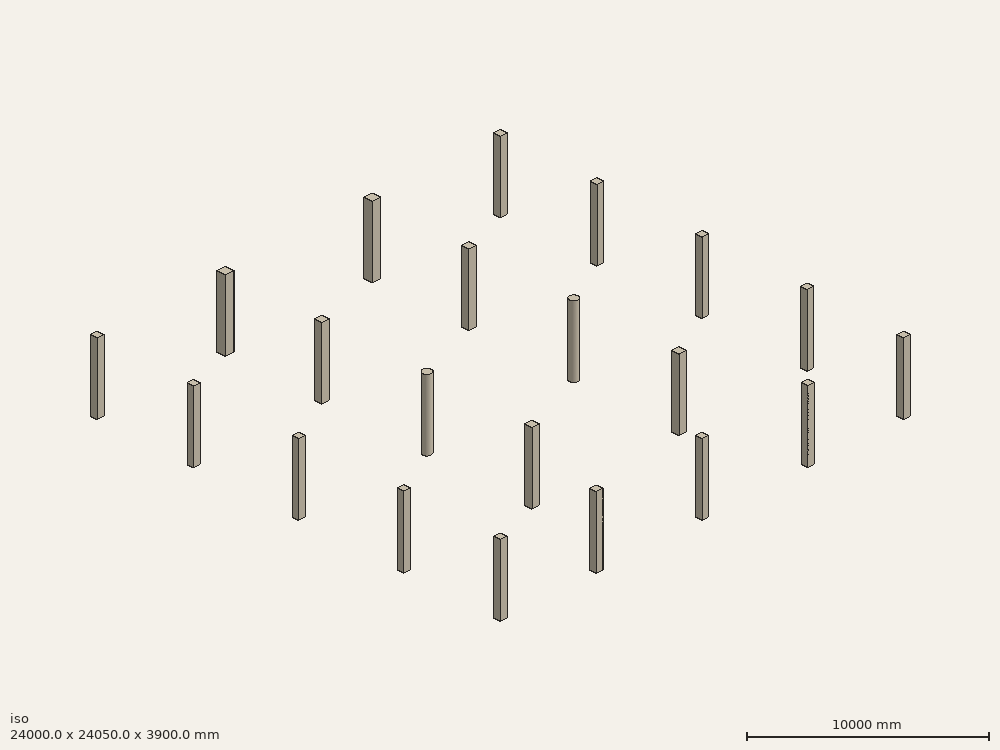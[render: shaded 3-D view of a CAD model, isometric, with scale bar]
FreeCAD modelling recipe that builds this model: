
FCSTD DOCUMENT  (FreeCAD 0.19R24291 (Git))
Label: Hamedan 1403
License: All rights reserved
LicenseURL: http://en.wikipedia.org/wiki/All_rights_reserved
objects: Part::Part2DObjectPython×82, Part::FeaturePython×65, App::FeaturePython×22, App::DocumentObjectGroup×5
note: 333 computed .brp shape members not serialized (recipe doc carries the construction recipe); baked Part::Feature solids carry a one-line shape summary decoded from their .brp

FEATURE [Part::Part2DObjectPython] Line  label="C21_Roof_CenterLine"  # Draft 2D object (typed FeaturePython)
  Area = 0
  ChamferSize = 0
  Closed = false
  End = (0,23600,3900)
  FilletRadius = 0
  Length = 3900
  MakeFace = true
  Points = (2) [(0,23600,0),(0,23600,3900)]
  Start = (0,23600,0)
  Subdivisions = 0
FEATURE [Part::Part2DObjectPython] C40X40_8T20  label="C40X40-8T20"  # Draft 2D object (typed FeaturePython)
  Height = 400
  Width = 400
FEATURE [Part::FeaturePython] Structure  label="C21_Roof"  # Arch/BIM 24 (typed FeaturePython)
  AttacherType = Attacher::AttachEngine3D
  AttachmentOffset = pos=(0,0,0) rot=(0,0,1;1.5708rad)
  Base = -> C40X40_8T20
  FaceMaker = 0
  Height = 3900
  HorizontalArea = 160000
  IfcData = attributes={"GlobalId": {"name": "GlobalId", "type": "IfcGloballyUniqueId", "is_enum": false, "enum_values": []}, "Description": {"... (+438 chars omitted),+1 more (map truncated)
  IfcType = 24
  Length = 0
  MapMode = 7
  MoveBase = false
  MoveWithHost = false
  Nodes = (2) [(0,23600,0),(0,23600,3900)]
  NodesOffset = 0
  Normal = (0,0,0)
  PerimeterLength = 1600
  Placement = pos=(0,23600,0) rot=(0,0,1;1.5708rad)
  PredefinedType = 0
  Support = -> [Line]
  VerticalArea = 6.24e+06
  Width = 100
  combos_load = COMB1 Max=142.9485, 1842.28, 55244.6,COMB10 Max=133.1342, -15451.88, 120563.4,COMB11 Max=142.7589, 32290.33, 117642.28,+33 more (map truncated)
FEATURE [Part::Part2DObjectPython] Line001  label="C22_Roof_CenterLine"  # Draft 2D object (typed FeaturePython)
  Area = 0
  ChamferSize = 0
  Closed = false
  End = (7500,23600,3900)
  FilletRadius = 0
  Length = 3900
  MakeFace = true
  Points = (2) [(7500,23600,0),(7500,23600,3900)]
  Start = (7500,23600,0)
  Subdivisions = 0
FEATURE [Part::Part2DObjectPython] C50X50_12T20  label="C50X50-12T20"  # Draft 2D object (typed FeaturePython)
  Height = 500
  Width = 500
FEATURE [Part::FeaturePython] Structure001  label="C22_Roof"  # Arch/BIM 24 (typed FeaturePython)
  AttacherType = Attacher::AttachEngine3D
  AttachmentOffset = pos=(0,0,0) rot=(0,0,1;1.5708rad)
  Base = -> C50X50_12T20
  FaceMaker = 0
  Height = 3900
  HorizontalArea = 250000
  IfcData = attributes={"GlobalId": {"name": "GlobalId", "type": "IfcGloballyUniqueId", "is_enum": false, "enum_values": []}, "Description": {"... (+438 chars omitted),+1 more (map truncated)
  IfcType = 24
  Length = 0
  MapMode = 7
  MoveBase = false
  MoveWithHost = false
  Nodes = (2) [(7500,23600,0),(7500,23600,3900)]
  NodesOffset = 0
  Normal = (0,0,0)
  PerimeterLength = 2000
  Placement = pos=(7500,23600,0) rot=(0,0,1;1.5708rad)
  PredefinedType = 0
  Support = -> [Line001]
  VerticalArea = 7.8e+06
  Width = 100
  combos_load = COMB1 Max=393.9617, -13954.51, 43208.61,COMB10 Max=364.0775, -60554.94, 217047.53,COMB11 Max=378.5992, 35975, 210039.05,+33 more (map truncated)
FEATURE [Part::Part2DObjectPython] Line002  label="C23_Roof_CenterLine"  # Draft 2D object (typed FeaturePython)
  Area = 0
  ChamferSize = 0
  Closed = false
  End = (16100,23600,3900)
  FilletRadius = 0
  Length = 3900
  MakeFace = true
  Points = (2) [(16100,23600,0),(16100,23600,3900)]
  Start = (16100,23600,0)
  Subdivisions = 0
FEATURE [Part::FeaturePython] Structure002  label="C23_Roof"  # Arch/BIM 24 (typed FeaturePython)
  AttacherType = Attacher::AttachEngine3D
  AttachmentOffset = pos=(0,0,0) rot=(0,0,1;1.5708rad)
  Base = -> C50X50_12T20
  FaceMaker = 0
  Height = 3900
  HorizontalArea = 250000
  IfcData = attributes={"GlobalId": {"name": "GlobalId", "type": "IfcGloballyUniqueId", "is_enum": false, "enum_values": []}, "Description": {"... (+438 chars omitted),+1 more (map truncated)
  IfcType = 24
  Length = 0
  MapMode = 7
  MoveBase = false
  MoveWithHost = false
  Nodes = (2) [(16100,23600,0),(16100,23600,3900)]
  NodesOffset = 0
  Normal = (0,0,0)
  PerimeterLength = 2000
  Placement = pos=(16100,23600,0) rot=(0,0,1;1.5708rad)
  PredefinedType = 0
  Support = -> [Line002]
  VerticalArea = 7.8e+06
  Width = 100
  combos_load = COMB1 Max=396.464, -11533.45, -20754.84,COMB10 Max=367.1221, -68059.63, 140987.04,COMB11 Max=381.1347, 24085.64, 134057.49,+33 more (map truncated)
FEATURE [Part::Part2DObjectPython] Line003  label="C24_Roof_CenterLine"  # Draft 2D object (typed FeaturePython)
  Area = 0
  ChamferSize = 0
  Closed = false
  End = (23600,23600,3900)
  FilletRadius = 0
  Length = 3900
  MakeFace = true
  Points = (2) [(23600,23600,0),(23600,23600,3900)]
  Start = (23600,23600,0)
  Subdivisions = 0
FEATURE [Part::FeaturePython] Structure003  label="C24_Roof"  # Arch/BIM 24 (typed FeaturePython)
  AttacherType = Attacher::AttachEngine3D
  AttachmentOffset = pos=(0,0,0) rot=(0,0,1;1.5708rad)
  Base = -> C40X40_8T20
  FaceMaker = 0
  Height = 3900
  HorizontalArea = 160000
  IfcData = attributes={"GlobalId": {"name": "GlobalId", "type": "IfcGloballyUniqueId", "is_enum": false, "enum_values": []}, "Description": {"... (+438 chars omitted),+1 more (map truncated)
  IfcType = 24
  Length = 0
  MapMode = 7
  MoveBase = false
  MoveWithHost = false
  Nodes = (2) [(23600,23600,0),(23600,23600,3900)]
  NodesOffset = 0
  Normal = (0,0,0)
  PerimeterLength = 1600
  Placement = pos=(23600,23600,0) rot=(0,0,1;1.5708rad)
  PredefinedType = 0
  Support = -> [Line003]
  VerticalArea = 6.24e+06
  Width = 100
  combos_load = COMB1 Max=153.397, 10863.78, -45811.62,COMB10 Max=112.4508, -20618.99, 32383.92,COMB11 Max=123.0217, 21926.74, 29412.84,+33 more (map truncated)
FEATURE [Part::Part2DObjectPython] Line004  label="C17_Roof_CenterLine"  # Draft 2D object (typed FeaturePython)
  Area = 0
  ChamferSize = 0
  Closed = false
  End = (0,17950,3900)
  FilletRadius = 0
  Length = 3900
  MakeFace = true
  Points = (2) [(0,17950,0),(0,17950,3900)]
  Start = (0,17950,0)
  Subdivisions = 0
FEATURE [Part::Part2DObjectPython] C40X40_12T25  label="C40X40-12T25"  # Draft 2D object (typed FeaturePython)
  Height = 400
  Width = 400
FEATURE [Part::FeaturePython] Structure004  label="C17_Roof"  # Arch/BIM 24 (typed FeaturePython)
  AttacherType = Attacher::AttachEngine3D
  AttachmentOffset = pos=(0,0,0) rot=(0,0,1;1.5708rad)
  Base = -> C40X40_12T25
  FaceMaker = 0
  Height = 3900
  HorizontalArea = 160000
  IfcData = attributes={"GlobalId": {"name": "GlobalId", "type": "IfcGloballyUniqueId", "is_enum": false, "enum_values": []}, "Description": {"... (+438 chars omitted),+1 more (map truncated)
  IfcType = 24
  Length = 0
  MapMode = 7
  MoveBase = false
  MoveWithHost = false
  Nodes = (2) [(0,17950,0),(0,17950,3900)]
  NodesOffset = 0
  Normal = (0,0,0)
  PerimeterLength = 1600
  Placement = pos=(0,17950,0) rot=(0,0,1;1.5708rad)
  PredefinedType = 0
  Support = -> [Line004]
  VerticalArea = 6.24e+06
  Width = 100
  combos_load = COMB1 Max=358.911, 57470.57, 72051.06,COMB10 Max=353.0021, 36535.59, 140227.2,COMB11 Max=363.1908, 99735.69, 139905.02,+33 more (map truncated)
FEATURE [Part::Part2DObjectPython] Line005  label="C18_Roof_CenterLine"  # Draft 2D object (typed FeaturePython)
  Area = 0
  ChamferSize = 0
  Closed = false
  End = (7500,17950,3900)
  FilletRadius = 0
  Length = 3900
  MakeFace = true
  Points = (2) [(7500,17950,0),(7500,17950,3900)]
  Start = (7500,17950,0)
  Subdivisions = 0
FEATURE [Part::Part2DObjectPython] C45X45_8T20  label="C45X45-8T20"  # Draft 2D object (typed FeaturePython)
  Height = 450
  Width = 450
FEATURE [Part::FeaturePython] Structure005  label="C18_Roof"  # Arch/BIM 24 (typed FeaturePython)
  AttacherType = Attacher::AttachEngine3D
  AttachmentOffset = pos=(0,0,0) rot=(0,0,1;1.5708rad)
  Base = -> C45X45_8T20
  FaceMaker = 0
  Height = 3900
  HorizontalArea = 202500
  IfcData = attributes={"GlobalId": {"name": "GlobalId", "type": "IfcGloballyUniqueId", "is_enum": false, "enum_values": []}, "Description": {"... (+438 chars omitted),+1 more (map truncated)
  IfcType = 24
  Length = 0
  MapMode = 7
  MoveBase = false
  MoveWithHost = false
  Nodes = (2) [(7500,17950,0),(7500,17950,3900)]
  NodesOffset = 0
  Normal = (0,0,0)
  PerimeterLength = 1800
  Placement = pos=(7500,17950,0) rot=(0,0,1;1.5708rad)
  PredefinedType = 0
  Support = -> [Line005]
  VerticalArea = 7.02e+06
  Width = 100
  combos_load = COMB1 Max=518.4758, 23786.04, 11881.46,COMB10 Max=465.1331, -14749.78, 131616.43,COMB11 Max=464.8478, 69418.5, 127330.18,+33 more (map truncated)
FEATURE [Part::Part2DObjectPython] Line006  label="C19_Roof_CenterLine"  # Draft 2D object (typed FeaturePython)
  Area = 0
  ChamferSize = 0
  Closed = false
  End = (16100,17950,3900)
  FilletRadius = 0
  Length = 3900
  MakeFace = true
  Points = (2) [(16100,17950,0),(16100,17950,3900)]
  Start = (16100,17950,0)
  Subdivisions = 0
FEATURE [Part::FeaturePython] Structure006  label="C19_Roof"  # Arch/BIM 24 (typed FeaturePython)
  AttacherType = Attacher::AttachEngine3D
  AttachmentOffset = pos=(0,0,0) rot=(0,0,1;1.5708rad)
  Base = -> C45X45_8T20
  FaceMaker = 0
  Height = 3900
  HorizontalArea = 202500
  IfcData = attributes={"GlobalId": {"name": "GlobalId", "type": "IfcGloballyUniqueId", "is_enum": false, "enum_values": []}, "Description": {"... (+438 chars omitted),+1 more (map truncated)
  IfcType = 24
  Length = 0
  MapMode = 7
  MoveBase = false
  MoveWithHost = false
  Nodes = (2) [(16100,17950,0),(16100,17950,3900)]
  NodesOffset = 0
  Normal = (0,0,0)
  PerimeterLength = 1800
  Placement = pos=(16100,17950,0) rot=(0,0,1;1.5708rad)
  PredefinedType = 0
  Support = -> [Line006]
  VerticalArea = 7.02e+06
  Width = 100
  combos_load = COMB1 Max=484.4175, 11062.32, -10447.14,COMB10 Max=434.4462, -34199.5, 113962.38,COMB11 Max=429.6664, 44640.41, 111093.37,+33 more (map truncated)
FEATURE [Part::Part2DObjectPython] Line007  label="C20_Roof_CenterLine"  # Draft 2D object (typed FeaturePython)
  Area = 0
  ChamferSize = 0
  Closed = false
  End = (23600,17950,3900)
  FilletRadius = 0
  Length = 3900
  MakeFace = true
  Points = (2) [(23600,17950,0),(23600,17950,3900)]
  Start = (23600,17950,0)
  Subdivisions = 0
FEATURE [Part::FeaturePython] Structure007  label="C20_Roof"  # Arch/BIM 24 (typed FeaturePython)
  AttacherType = Attacher::AttachEngine3D
  AttachmentOffset = pos=(0,0,0) rot=(0,0,1;1.5708rad)
  Base = -> C40X40_8T20
  FaceMaker = 0
  Height = 3900
  HorizontalArea = 160000
  IfcData = attributes={"GlobalId": {"name": "GlobalId", "type": "IfcGloballyUniqueId", "is_enum": false, "enum_values": []}, "Description": {"... (+438 chars omitted),+1 more (map truncated)
  IfcType = 24
  Length = 0
  MapMode = 7
  MoveBase = false
  MoveWithHost = false
  Nodes = (2) [(23600,17950,0),(23600,17950,3900)]
  NodesOffset = 0
  Normal = (0,0,0)
  PerimeterLength = 1600
  Placement = pos=(23600,17950,0) rot=(0,0,1;1.5708rad)
  PredefinedType = 0
  Support = -> [Line007]
  VerticalArea = 6.24e+06
  Width = 100
  combos_load = COMB1 Max=278.7163, 9412.13, -69745.5,COMB10 Max=243.1734, -24585.97, 13268.13,COMB11 Max=240.9121, 26667.65, 11896.36,+33 more (map truncated)
FEATURE [Part::Part2DObjectPython] Line008  label="C10_Roof_CenterLine"  # Draft 2D object (typed FeaturePython)
  Area = 0
  ChamferSize = 0
  Closed = false
  End = (0,11800,3900)
  FilletRadius = 0
  Length = 3900
  MakeFace = true
  Points = (2) [(0,11800,0),(0,11800,3900)]
  Start = (0,11800,0)
  Subdivisions = 0
FEATURE [Part::Part2DObjectPython] C40X40_14T25  label="C40X40-14T25"  # Draft 2D object (typed FeaturePython)
  Height = 400
  Width = 400
FEATURE [Part::FeaturePython] Structure008  label="C10_Roof"  # Arch/BIM 24 (typed FeaturePython)
  AttacherType = Attacher::AttachEngine3D
  AttachmentOffset = pos=(0,0,0) rot=(0,0,1;1.5708rad)
  Base = -> C40X40_14T25
  FaceMaker = 0
  Height = 3900
  HorizontalArea = 160000
  IfcData = attributes={"GlobalId": {"name": "GlobalId", "type": "IfcGloballyUniqueId", "is_enum": false, "enum_values": []}, "Description": {"... (+438 chars omitted),+1 more (map truncated)
  IfcType = 24
  Length = 0
  MapMode = 7
  MoveBase = false
  MoveWithHost = false
  Nodes = (2) [(0,11800,0),(0,11800,3900)]
  NodesOffset = 0
  Normal = (0,0,0)
  PerimeterLength = 1600
  Placement = pos=(0,11800,0) rot=(0,0,1;1.5708rad)
  PredefinedType = 0
  Support = -> [Line008]
  VerticalArea = 6.24e+06
  Width = 100
  combos_load = COMB1 Max=589.8541, -52928.2, 64357.09,COMB10 Max=631.112, -70198.61, 138253.26,COMB11 Max=620.3172, -15825.73, 137456.82,+33 more (map truncated)
FEATURE [Part::Part2DObjectPython] Line009  label="C12_Roof_CenterLine"  # Draft 2D object (typed FeaturePython)
  Area = 0
  ChamferSize = 0
  Closed = false
  End = (7500,11800,3900)
  FilletRadius = 0
  Length = 3900
  MakeFace = true
  Points = (2) [(7500,11800,0),(7500,11800,3900)]
  Start = (7500,11800,0)
  Subdivisions = 0
FEATURE [Part::Part2DObjectPython] Circle  label="CC50-10T20"  # Draft 2D object (typed FeaturePython)
  Area = 196350
  FirstAngle = 0
  LastAngle = 0
  MakeFace = true
  Radius = 250
FEATURE [Part::FeaturePython] Structure009  label="C12_Roof"  # Arch/BIM 24 (typed FeaturePython)
  AttacherType = Attacher::AttachEngine3D
  AttachmentOffset = pos=(0,0,0) rot=(0,0,1;1.5708rad)
  Base = -> Circle
  FaceMaker = 0
  Height = 3900
  HorizontalArea = 196350
  IfcData = attributes={"GlobalId": {"name": "GlobalId", "type": "IfcGloballyUniqueId", "is_enum": false, "enum_values": []}, "Description": {"... (+438 chars omitted),+1 more (map truncated)
  IfcType = 24
  Length = 0
  MapMode = 7
  MoveBase = false
  MoveWithHost = false
  Nodes = (2) [(7500,11800,0),(7500,11800,3900)]
  NodesOffset = 0
  Normal = (0,0,0)
  PerimeterLength = 1570.8
  Placement = pos=(7500,11800,0) rot=(0,0,1;1.5708rad)
  PredefinedType = 0
  Support = -> [Line009]
  VerticalArea = 6.12611e+06
  Width = 100
  combos_load = COMB1 Max=671.1533, -4639.28, -19744.15,COMB10 Max=592.2997, -35909.44, 99080.12,COMB11 Max=588.052, 37558.56, 101179.49,+33 more (map truncated)
FEATURE [Part::Part2DObjectPython] Line010  label="C13_Roof_CenterLine"  # Draft 2D object (typed FeaturePython)
  Area = 0
  ChamferSize = 0
  Closed = false
  End = (16100,11800,3900)
  FilletRadius = 0
  Length = 3900
  MakeFace = true
  Points = (2) [(16100,11800,0),(16100,11800,3900)]
  Start = (16100,11800,0)
  Subdivisions = 0
FEATURE [Part::FeaturePython] Structure010  label="C13_Roof"  # Arch/BIM 24 (typed FeaturePython)
  AttacherType = Attacher::AttachEngine3D
  AttachmentOffset = pos=(0,0,0) rot=(0,0,1;1.5708rad)
  Base = -> Circle
  FaceMaker = 0
  Height = 3900
  HorizontalArea = 196350
  IfcData = attributes={"GlobalId": {"name": "GlobalId", "type": "IfcGloballyUniqueId", "is_enum": false, "enum_values": []}, "Description": {"... (+438 chars omitted),+1 more (map truncated)
  IfcType = 24
  Length = 0
  MapMode = 7
  MoveBase = false
  MoveWithHost = false
  Nodes = (2) [(16100,11800,0),(16100,11800,3900)]
  NodesOffset = 0
  Normal = (0,0,0)
  PerimeterLength = 1570.8
  Placement = pos=(16100,11800,0) rot=(0,0,1;1.5708rad)
  PredefinedType = 0
  Support = -> [Line010]
  VerticalArea = 6.12611e+06
  Width = 100
  combos_load = COMB1 Max=521.6342, 3870.36, -23693.9,COMB10 Max=463.3802, -36720.59, 97522.75,COMB11 Max=463.6235, 33841.58, 97587.97,+33 more (map truncated)
FEATURE [Part::Part2DObjectPython] Line011  label="C14_Roof_CenterLine"  # Draft 2D object (typed FeaturePython)
  Area = 0
  ChamferSize = 0
  Closed = false
  End = (23600,11800,3900)
  FilletRadius = 0
  Length = 3900
  MakeFace = true
  Points = (2) [(23600,11800,0),(23600,11800,3900)]
  Start = (23600,11800,0)
  Subdivisions = 0
FEATURE [Part::FeaturePython] Structure011  label="C14_Roof"  # Arch/BIM 24 (typed FeaturePython)
  AttacherType = Attacher::AttachEngine3D
  AttachmentOffset = pos=(0,0,0) rot=(0,0,1;1.5708rad)
  Base = -> C40X40_8T20
  FaceMaker = 0
  Height = 3900
  HorizontalArea = 160000
  IfcData = attributes={"GlobalId": {"name": "GlobalId", "type": "IfcGloballyUniqueId", "is_enum": false, "enum_values": []}, "Description": {"... (+438 chars omitted),+1 more (map truncated)
  IfcType = 24
  Length = 0
  MapMode = 7
  MoveBase = false
  MoveWithHost = false
  Nodes = (2) [(23600,11800,0),(23600,11800,3900)]
  NodesOffset = 0
  Normal = (0,0,0)
  PerimeterLength = 1600
  Placement = pos=(23600,11800,0) rot=(0,0,1;1.5708rad)
  PredefinedType = 0
  Support = -> [Line011]
  VerticalArea = 6.24e+06
  Width = 100
  combos_load = COMB1 Max=358.2322, 3461.97, -48336.62,COMB10 Max=334.417, -31946.94, 41113.22,COMB11 Max=334.4426, 18858.68, 41094.62,+33 more (map truncated)
FEATURE [Part::Part2DObjectPython] Line012  label="C6_Roof_CenterLine"  # Draft 2D object (typed FeaturePython)
  Area = 0
  ChamferSize = 0
  Closed = false
  End = (0,5650,3900)
  FilletRadius = 0
  Length = 3900
  MakeFace = true
  Points = (2) [(0,5650,0),(0,5650,3900)]
  Start = (0,5650,0)
  Subdivisions = 0
FEATURE [Part::FeaturePython] Structure012  label="C6_Roof"  # Arch/BIM 24 (typed FeaturePython)
  AttacherType = Attacher::AttachEngine3D
  AttachmentOffset = pos=(0,0,0) rot=(0,0,1;1.5708rad)
  Base = -> C40X40_12T25
  FaceMaker = 0
  Height = 3900
  HorizontalArea = 160000
  IfcData = attributes={"GlobalId": {"name": "GlobalId", "type": "IfcGloballyUniqueId", "is_enum": false, "enum_values": []}, "Description": {"... (+438 chars omitted),+1 more (map truncated)
  IfcType = 24
  Length = 0
  MapMode = 7
  MoveBase = false
  MoveWithHost = false
  Nodes = (2) [(0,5650,0),(0,5650,3900)]
  NodesOffset = 0
  Normal = (0,0,0)
  PerimeterLength = 1600
  Placement = pos=(0,5650,0) rot=(0,0,1;1.5708rad)
  PredefinedType = 0
  Support = -> [Line012]
  VerticalArea = 6.24e+06
  Width = 100
  combos_load = COMB1 Max=262.5559, 5891.08, 79097.96,COMB10 Max=251.8265, -15804.53, 150501.97,COMB11 Max=253.791, 43165.94, 152334.32,+33 more (map truncated)
FEATURE [Part::Part2DObjectPython] Line013  label="C7_Roof_CenterLine"  # Draft 2D object (typed FeaturePython)
  Area = 0
  ChamferSize = 0
  Closed = false
  End = (7500,5650,3900)
  FilletRadius = 0
  Length = 3900
  MakeFace = true
  Points = (2) [(7500,5650,0),(7500,5650,3900)]
  Start = (7500,5650,0)
  Subdivisions = 0
FEATURE [Part::FeaturePython] Structure013  label="C7_Roof"  # Arch/BIM 24 (typed FeaturePython)
  AttacherType = Attacher::AttachEngine3D
  AttachmentOffset = pos=(0,0,0) rot=(0,0,1;1.5708rad)
  Base = -> C45X45_8T20
  FaceMaker = 0
  Height = 3900
  HorizontalArea = 202500
  IfcData = attributes={"GlobalId": {"name": "GlobalId", "type": "IfcGloballyUniqueId", "is_enum": false, "enum_values": []}, "Description": {"... (+438 chars omitted),+1 more (map truncated)
  IfcType = 24
  Length = 0
  MapMode = 7
  MoveBase = false
  MoveWithHost = false
  Nodes = (2) [(7500,5650,0),(7500,5650,3900)]
  NodesOffset = 0
  Normal = (0,0,0)
  PerimeterLength = 1800
  Placement = pos=(7500,5650,0) rot=(0,0,1;1.5708rad)
  PredefinedType = 0
  Support = -> [Line013]
  VerticalArea = 7.02e+06
  Width = 100
  combos_load = COMB1 Max=486.3324, 7340.08, 20569.07,COMB10 Max=420.769, -32429.99, 154764.38,COMB11 Max=424.0342, 47843.18, 155600.42,+33 more (map truncated)
FEATURE [Part::Part2DObjectPython] Line014  label="C8_Roof_CenterLine"  # Draft 2D object (typed FeaturePython)
  Area = 0
  ChamferSize = 0
  Closed = false
  End = (16100,5650,3900)
  FilletRadius = 0
  Length = 3900
  MakeFace = true
  Points = (2) [(16100,5650,0),(16100,5650,3900)]
  Start = (16100,5650,0)
  Subdivisions = 0
FEATURE [Part::FeaturePython] Structure014  label="C8_Roof"  # Arch/BIM 24 (typed FeaturePython)
  AttacherType = Attacher::AttachEngine3D
  AttachmentOffset = pos=(0,0,0) rot=(0,0,1;1.5708rad)
  Base = -> C45X45_8T20
  FaceMaker = 0
  Height = 3900
  HorizontalArea = 202500
  IfcData = attributes={"GlobalId": {"name": "GlobalId", "type": "IfcGloballyUniqueId", "is_enum": false, "enum_values": []}, "Description": {"... (+438 chars omitted),+1 more (map truncated)
  IfcType = 24
  Length = 0
  MapMode = 7
  MoveBase = false
  MoveWithHost = false
  Nodes = (2) [(16100,5650,0),(16100,5650,3900)]
  NodesOffset = 0
  Normal = (0,0,0)
  PerimeterLength = 1800
  Placement = pos=(16100,5650,0) rot=(0,0,1;1.5708rad)
  PredefinedType = 0
  Support = -> [Line014]
  VerticalArea = 7.02e+06
  Width = 100
  combos_load = COMB1 Max=488.6288, 6936.79, -6872.61,COMB10 Max=436.9461, -33228.07, 129912.68,COMB11 Max=440.3998, 43388.79, 134096.59,+33 more (map truncated)
FEATURE [Part::Part2DObjectPython] Line015  label="C9_Roof_CenterLine"  # Draft 2D object (typed FeaturePython)
  Area = 0
  ChamferSize = 0
  Closed = false
  End = (23600,5650,3900)
  FilletRadius = 0
  Length = 3900
  MakeFace = true
  Points = (2) [(23600,5650,0),(23600,5650,3900)]
  Start = (23600,5650,0)
  Subdivisions = 0
FEATURE [Part::FeaturePython] Structure015  label="C9_Roof"  # Arch/BIM 24 (typed FeaturePython)
  AttacherType = Attacher::AttachEngine3D
  AttachmentOffset = pos=(0,0,0) rot=(0,0,1;1.5708rad)
  Base = -> C40X40_8T20
  FaceMaker = 0
  Height = 3900
  HorizontalArea = 160000
  IfcData = attributes={"GlobalId": {"name": "GlobalId", "type": "IfcGloballyUniqueId", "is_enum": false, "enum_values": []}, "Description": {"... (+438 chars omitted),+1 more (map truncated)
  IfcType = 24
  Length = 0
  MapMode = 7
  MoveBase = false
  MoveWithHost = false
  Nodes = (2) [(23600,5650,0),(23600,5650,3900)]
  NodesOffset = 0
  Normal = (0,0,0)
  PerimeterLength = 1600
  Placement = pos=(23600,5650,0) rot=(0,0,1;1.5708rad)
  PredefinedType = 0
  Support = -> [Line015]
  VerticalArea = 6.24e+06
  Width = 100
  combos_load = COMB1 Max=279.2867, -2196.26, -68861.03,COMB10 Max=239.3362, -39528.22, 20968.97,COMB11 Max=241.6585, 11663.57, 22200.49,+33 more (map truncated)
FEATURE [Part::Part2DObjectPython] Line016  label="C1_Roof_CenterLine"  # Draft 2D object (typed FeaturePython)
  Area = 0
  ChamferSize = 0
  Closed = false
  End = (0,0,3900)
  FilletRadius = 0
  Length = 3900
  MakeFace = true
  Points = (2) [(0,0,0),(0,0,3900)]
  Start = (0,0,0)
  Subdivisions = 0
FEATURE [Part::FeaturePython] Structure016  label="C1_Roof"  # Arch/BIM 24 (typed FeaturePython)
  AttacherType = Attacher::AttachEngine3D
  AttachmentOffset = pos=(0,0,0) rot=(0,0,1;1.5708rad)
  Base = -> C40X40_8T20
  FaceMaker = 0
  Height = 3900
  HorizontalArea = 160000
  IfcData = attributes={"GlobalId": {"name": "GlobalId", "type": "IfcGloballyUniqueId", "is_enum": false, "enum_values": []}, "Description": {"... (+438 chars omitted),+1 more (map truncated)
  IfcType = 24
  Length = 0
  MapMode = 7
  MoveBase = false
  MoveWithHost = false
  Nodes = (2) [(0,0,0),(0,0,3900)]
  NodesOffset = 0
  Normal = (0,0,0)
  PerimeterLength = 1600
  Placement = pos=(0,0,0) rot=(0,0,1;1.5708rad)
  PredefinedType = 0
  Support = -> [Line016]
  VerticalArea = 6.24e+06
  Width = 100
  combos_load = COMB1 Max=128.3129, -7400.35, 32963.08,COMB10 Max=134.9498, -22111.65, 115539.05,COMB11 Max=125.0545, 26595.57, 119011.72,+33 more (map truncated)
FEATURE [Part::Part2DObjectPython] Line017  label="C2_Roof_CenterLine"  # Draft 2D object (typed FeaturePython)
  Area = 0
  ChamferSize = 0
  Closed = false
  End = (5600,0,3900)
  FilletRadius = 0
  Length = 3900
  MakeFace = true
  Points = (2) [(5600,0,0),(5600,0,3900)]
  Start = (5600,0,0)
  Subdivisions = 0
FEATURE [Part::FeaturePython] Structure017  label="C2_Roof"  # Arch/BIM 24 (typed FeaturePython)
  AttacherType = Attacher::AttachEngine3D
  AttachmentOffset = pos=(0,0,0) rot=(0,0,1;1.5708rad)
  Base = -> C40X40_8T20
  FaceMaker = 0
  Height = 3900
  HorizontalArea = 160000
  IfcData = attributes={"GlobalId": {"name": "GlobalId", "type": "IfcGloballyUniqueId", "is_enum": false, "enum_values": []}, "Description": {"... (+438 chars omitted),+1 more (map truncated)
  IfcType = 24
  Length = 0
  MapMode = 7
  MoveBase = false
  MoveWithHost = false
  Nodes = (2) [(5600,0,0),(5600,0,3900)]
  NodesOffset = 0
  Normal = (0,0,0)
  PerimeterLength = 1600
  Placement = pos=(5600,0,0) rot=(0,0,1;1.5708rad)
  PredefinedType = 0
  Support = -> [Line017]
  VerticalArea = 6.24e+06
  Width = 100
  combos_load = COMB1 Max=252.552, -5174.66, 11238.32,COMB10 Max=233.652, -25414.37, 117718.02,COMB11 Max=222.797, 20756.94, 118967.53,+33 more (map truncated)
FEATURE [Part::Part2DObjectPython] Line018  label="C3_Roof_CenterLine"  # Draft 2D object (typed FeaturePython)
  Area = 0
  ChamferSize = 0
  Closed = false
  End = (11800,0,3900)
  FilletRadius = 0
  Length = 3900
  MakeFace = true
  Points = (2) [(11800,0,0),(11800,0,3900)]
  Start = (11800,0,0)
  Subdivisions = 0
FEATURE [Part::FeaturePython] Structure018  label="C3_Roof"  # Arch/BIM 24 (typed FeaturePython)
  AttacherType = Attacher::AttachEngine3D
  AttachmentOffset = pos=(0,0,0) rot=(0,0,1;1.5708rad)
  Base = -> C40X40_8T20
  FaceMaker = 0
  Height = 3900
  HorizontalArea = 160000
  IfcData = attributes={"GlobalId": {"name": "GlobalId", "type": "IfcGloballyUniqueId", "is_enum": false, "enum_values": []}, "Description": {"... (+438 chars omitted),+1 more (map truncated)
  IfcType = 24
  Length = 0
  MapMode = 7
  MoveBase = false
  MoveWithHost = false
  Nodes = (2) [(11800,0,0),(11800,0,3900)]
  NodesOffset = 0
  Normal = (0,0,0)
  PerimeterLength = 1600
  Placement = pos=(11800,0,0) rot=(0,0,1;1.5708rad)
  PredefinedType = 0
  Support = -> [Line018]
  VerticalArea = 6.24e+06
  Width = 100
  combos_load = COMB1 Max=348.9502, -371.51, 5629.95,COMB10 Max=343.0875, -13644.77, 109460.45,COMB11 Max=336.1426, 28367.03, 113069.54,+33 more (map truncated)
FEATURE [Part::Part2DObjectPython] Line019  label="C4_Roof_CenterLine"  # Draft 2D object (typed FeaturePython)
  Area = 0
  ChamferSize = 0
  Closed = false
  End = (18000,0,3900)
  FilletRadius = 0
  Length = 3900
  MakeFace = true
  Points = (2) [(18000,0,0),(18000,0,3900)]
  Start = (18000,0,0)
  Subdivisions = 0
FEATURE [Part::FeaturePython] Structure019  label="C4_Roof"  # Arch/BIM 24 (typed FeaturePython)
  AttacherType = Attacher::AttachEngine3D
  AttachmentOffset = pos=(0,0,0) rot=(0,0,1;1.5708rad)
  Base = -> C40X40_8T20
  FaceMaker = 0
  Height = 3900
  HorizontalArea = 160000
  IfcData = attributes={"GlobalId": {"name": "GlobalId", "type": "IfcGloballyUniqueId", "is_enum": false, "enum_values": []}, "Description": {"... (+438 chars omitted),+1 more (map truncated)
  IfcType = 24
  Length = 0
  MapMode = 7
  MoveBase = false
  MoveWithHost = false
  Nodes = (2) [(18000,0,0),(18000,0,3900)]
  NodesOffset = 0
  Normal = (0,0,0)
  PerimeterLength = 1600
  Placement = pos=(18000,0,0) rot=(0,0,1;1.5708rad)
  PredefinedType = 0
  Support = -> [Line019]
  VerticalArea = 6.24e+06
  Width = 100
  combos_load = COMB1 Max=252.5212, -4382.88, -22.4,COMB10 Max=239.2844, -24091.04, 100756.71,COMB11 Max=229.2417, 19204.23, 106588.24,+33 more (map truncated)
FEATURE [Part::Part2DObjectPython] Line020  label="C5_Roof_CenterLine"  # Draft 2D object (typed FeaturePython)
  Area = 0
  ChamferSize = 0
  Closed = false
  End = (23600,0,3900)
  FilletRadius = 0
  Length = 3900
  MakeFace = true
  Points = (2) [(23600,0,0),(23600,0,3900)]
  Start = (23600,0,0)
  Subdivisions = 0
FEATURE [Part::FeaturePython] Structure020  label="C5_Roof"  # Arch/BIM 24 (typed FeaturePython)
  AttacherType = Attacher::AttachEngine3D
  AttachmentOffset = pos=(0,0,0) rot=(0,0,1;1.5708rad)
  Base = -> C40X40_8T20
  FaceMaker = 0
  Height = 3900
  HorizontalArea = 160000
  IfcData = attributes={"GlobalId": {"name": "GlobalId", "type": "IfcGloballyUniqueId", "is_enum": false, "enum_values": []}, "Description": {"... (+438 chars omitted),+1 more (map truncated)
  IfcType = 24
  Length = 0
  MapMode = 7
  MoveBase = false
  MoveWithHost = false
  Nodes = (2) [(23600,0,0),(23600,0,3900)]
  NodesOffset = 0
  Normal = (0,0,0)
  PerimeterLength = 1600
  Placement = pos=(23600,0,0) rot=(0,0,1;1.5708rad)
  PredefinedType = 0
  Support = -> [Line020]
  VerticalArea = 6.24e+06
  Width = 100
  combos_load = COMB1 Max=123.9264, -5590.09, -23570.29,COMB10 Max=93.1458, -33565.88, 66920.13,COMB11 Max=83.0591, 9199.66, 69526.94,+33 more (map truncated)
FEATURE [App::DocumentObjectGroup] Columns
  Group = -> [Structure,Structure001,Structure002,Structure003,Structure004,Structure005,Structure006,Structure007,Structure008,Structure009,Structure010,Structure011,Structure012,Structure013,Structure014,Structure015,Structure016,Structure017,Structure018,Structure019,Structure020]
FEATURE [Part::Part2DObjectPython] Line021  # Draft 2D object (typed FeaturePython)
  Area = 0
  ChamferSize = 0
  Closed = false
  End = (7500,23600,0)
  FilletRadius = 0
  Length = 7500
  MakeFace = true
  Points = (2) [(0,23600,0),(7500,23600,0)]
  Start = (0,23600,0)
  Subdivisions = 0
  type = Beam
FEATURE [Part::Part2DObjectPython] Line022  # Draft 2D object (typed FeaturePython)
  Area = 0
  ChamferSize = 0
  Closed = false
  End = (16100,23600,0)
  FilletRadius = 0
  Length = 8600
  MakeFace = true
  Points = (2) [(7500,23600,0),(16100,23600,0)]
  Start = (7500,23600,0)
  Subdivisions = 0
  type = Beam
FEATURE [Part::Part2DObjectPython] Line023  # Draft 2D object (typed FeaturePython)
  Area = 0
  ChamferSize = 0
  Closed = false
  End = (23600,23600,0)
  FilletRadius = 0
  Length = 7500
  MakeFace = true
  Points = (2) [(16100,23600,0),(23600,23600,0)]
  Start = (16100,23600,0)
  Subdivisions = 0
  type = Beam
FEATURE [Part::Part2DObjectPython] Line024  # Draft 2D object (typed FeaturePython)
  Area = 0
  ChamferSize = 0
  Closed = false
  End = (7500,17950,0)
  FilletRadius = 0
  Length = 7500
  MakeFace = true
  Points = (2) [(0,17950,0),(7500,17950,0)]
  Start = (0,17950,0)
  Subdivisions = 0
  type = Beam
FEATURE [Part::Part2DObjectPython] Line025  # Draft 2D object (typed FeaturePython)
  Area = 0
  ChamferSize = 0
  Closed = false
  End = (16100,17950,0)
  FilletRadius = 0
  Length = 8600
  MakeFace = true
  Points = (2) [(7500,17950,0),(16100,17950,0)]
  Start = (7500,17950,0)
  Subdivisions = 0
  type = Beam
FEATURE [Part::Part2DObjectPython] Line026  # Draft 2D object (typed FeaturePython)
  Area = 0
  ChamferSize = 0
  Closed = false
  End = (23600,17950,0)
  FilletRadius = 0
  Length = 7500
  MakeFace = true
  Points = (2) [(16100,17950,0),(23600,17950,0)]
  Start = (16100,17950,0)
  Subdivisions = 0
  type = Beam
FEATURE [Part::Part2DObjectPython] Line027  # Draft 2D object (typed FeaturePython)
  Area = 0
  ChamferSize = 0
  Closed = false
  End = (7500,11800,0)
  FilletRadius = 0
  Length = 7500
  MakeFace = true
  Points = (2) [(0,11800,0),(7500,11800,0)]
  Start = (0,11800,0)
  Subdivisions = 0
  type = Beam
FEATURE [Part::Part2DObjectPython] Line028  # Draft 2D object (typed FeaturePython)
  Area = 0
  ChamferSize = 0
  Closed = false
  End = (16100,11800,0)
  FilletRadius = 0
  Length = 8600
  MakeFace = true
  Points = (2) [(7500,11800,0),(16100,11800,0)]
  Start = (7500,11800,0)
  Subdivisions = 0
  type = Beam
FEATURE [Part::Part2DObjectPython] Line029  # Draft 2D object (typed FeaturePython)
  Area = 0
  ChamferSize = 0
  Closed = false
  End = (23600,11800,0)
  FilletRadius = 0
  Length = 7500
  MakeFace = true
  Points = (2) [(16100,11800,0),(23600,11800,0)]
  Start = (16100,11800,0)
  Subdivisions = 0
  type = Beam
FEATURE [Part::Part2DObjectPython] Line030  # Draft 2D object (typed FeaturePython)
  Area = 0
  ChamferSize = 0
  Closed = false
  End = (7500,5650,0)
  FilletRadius = 0
  Length = 7500
  MakeFace = true
  Points = (2) [(0,5650,0),(7500,5650,0)]
  Start = (0,5650,0)
  Subdivisions = 0
  type = Beam
FEATURE [Part::Part2DObjectPython] Line031  # Draft 2D object (typed FeaturePython)
  Area = 0
  ChamferSize = 0
  Closed = false
  End = (16100,5650,0)
  FilletRadius = 0
  Length = 8600
  MakeFace = true
  Points = (2) [(7500,5650,0),(16100,5650,0)]
  Start = (7500,5650,0)
  Subdivisions = 0
  type = Beam
FEATURE [Part::Part2DObjectPython] Line032  # Draft 2D object (typed FeaturePython)
  Area = 0
  ChamferSize = 0
  Closed = false
  End = (23600,5650,0)
  FilletRadius = 0
  Length = 7500
  MakeFace = true
  Points = (2) [(16100,5650,0),(23600,5650,0)]
  Start = (16100,5650,0)
  Subdivisions = 0
  type = Beam
FEATURE [Part::Part2DObjectPython] Line033  # Draft 2D object (typed FeaturePython)
  Area = 0
  ChamferSize = 0
  Closed = false
  End = (5600,0,0)
  FilletRadius = 0
  Length = 5600
  MakeFace = true
  Points = (2) [(0,0,0),(5600,0,0)]
  Start = (0,0,0)
  Subdivisions = 0
  type = Beam
FEATURE [Part::Part2DObjectPython] Line034  # Draft 2D object (typed FeaturePython)
  Area = 0
  ChamferSize = 0
  Closed = false
  End = (11800,0,0)
  FilletRadius = 0
  Length = 6200
  MakeFace = true
  Points = (2) [(5600,0,0),(11800,0,0)]
  Start = (5600,0,0)
  Subdivisions = 0
  type = Beam
FEATURE [Part::Part2DObjectPython] Line035  # Draft 2D object (typed FeaturePython)
  Area = 0
  ChamferSize = 0
  Closed = false
  End = (18000,0,0)
  FilletRadius = 0
  Length = 6200
  MakeFace = true
  Points = (2) [(11800,0,0),(18000,0,0)]
  Start = (11800,0,0)
  Subdivisions = 0
  type = Beam
FEATURE [Part::Part2DObjectPython] Line036  # Draft 2D object (typed FeaturePython)
  Area = 0
  ChamferSize = 0
  Closed = false
  End = (23600,0,0)
  FilletRadius = 0
  Length = 5600
  MakeFace = true
  Points = (2) [(18000,0,0),(23600,0,0)]
  Start = (18000,0,0)
  Subdivisions = 0
  type = Beam
FEATURE [Part::Part2DObjectPython] Line037  # Draft 2D object (typed FeaturePython)
  Area = 0
  ChamferSize = 0
  Closed = false
  End = (23600,5650,0)
  FilletRadius = 0
  Length = 5650
  MakeFace = true
  Points = (2) [(23600,0,0),(23600,5650,0)]
  Start = (23600,0,0)
  Subdivisions = 0
  type = Beam
FEATURE [Part::Part2DObjectPython] Line038  # Draft 2D object (typed FeaturePython)
  Area = 0
  ChamferSize = 0
  Closed = false
  End = (23600,11800,0)
  FilletRadius = 0
  Length = 6150
  MakeFace = true
  Points = (2) [(23600,5650,0),(23600,11800,0)]
  Start = (23600,5650,0)
  Subdivisions = 0
  type = Beam
FEATURE [Part::Part2DObjectPython] Line039  # Draft 2D object (typed FeaturePython)
  Area = 0
  ChamferSize = 0
  Closed = false
  End = (23600,17950,0)
  FilletRadius = 0
  Length = 6150
  MakeFace = true
  Points = (2) [(23600,11800,0),(23600,17950,0)]
  Start = (23600,11800,0)
  Subdivisions = 0
  type = Beam
FEATURE [Part::Part2DObjectPython] Line040  # Draft 2D object (typed FeaturePython)
  Area = 0
  ChamferSize = 0
  Closed = false
  End = (23600,23600,0)
  FilletRadius = 0
  Length = 5650
  MakeFace = true
  Points = (2) [(23600,17950,0),(23600,23600,0)]
  Start = (23600,17950,0)
  Subdivisions = 0
  type = Beam
FEATURE [Part::Part2DObjectPython] Line041  # Draft 2D object (typed FeaturePython)
  Area = 0
  ChamferSize = 0
  Closed = false
  End = (0,5650,0)
  FilletRadius = 0
  Length = 5650
  MakeFace = true
  Points = (2) [(0,0,0),(0,5650,0)]
  Start = (0,0,0)
  Subdivisions = 0
  type = Beam
FEATURE [Part::Part2DObjectPython] Line042  # Draft 2D object (typed FeaturePython)
  Area = 0
  ChamferSize = 0
  Closed = false
  End = (0,11800,0)
  FilletRadius = 0
  Length = 6150
  MakeFace = true
  Points = (2) [(0,5650,0),(0,11800,0)]
  Start = (0,5650,0)
  Subdivisions = 0
  type = Beam
FEATURE [Part::Part2DObjectPython] Line043  # Draft 2D object (typed FeaturePython)
  Area = 0
  ChamferSize = 0
  Closed = false
  End = (0,17950,0)
  FilletRadius = 0
  Length = 6150
  MakeFace = true
  Points = (2) [(0,11800,0),(0,17950,0)]
  Start = (0,11800,0)
  Subdivisions = 0
  type = Beam
FEATURE [Part::Part2DObjectPython] Line044  # Draft 2D object (typed FeaturePython)
  Area = 0
  ChamferSize = 0
  Closed = false
  End = (0,23600,0)
  FilletRadius = 0
  Length = 5650
  MakeFace = true
  Points = (2) [(0,17950,0),(0,23600,0)]
  Start = (0,17950,0)
  Subdivisions = 0
  type = Beam
FEATURE [Part::Part2DObjectPython] Line045  # Draft 2D object (typed FeaturePython)
  Area = 0
  ChamferSize = 0
  Closed = false
  End = (7500,5650,0)
  FilletRadius = 0
  Length = 5960.91
  MakeFace = true
  Points = (2) [(5600,0,0),(7500,5650,0)]
  Start = (5600,0,0)
  Subdivisions = 0
  type = Beam
FEATURE [Part::Part2DObjectPython] Line046  # Draft 2D object (typed FeaturePython)
  Area = 0
  ChamferSize = 0
  Closed = false
  End = (7500,11800,0)
  FilletRadius = 0
  Length = 6150
  MakeFace = true
  Points = (2) [(7500,5650,0),(7500,11800,0)]
  Start = (7500,5650,0)
  Subdivisions = 0
  type = Beam
FEATURE [Part::Part2DObjectPython] Line047  # Draft 2D object (typed FeaturePython)
  Area = 0
  ChamferSize = 0
  Closed = false
  End = (7500,17950,0)
  FilletRadius = 0
  Length = 6150
  MakeFace = true
  Points = (2) [(7500,11800,0),(7500,17950,0)]
  Start = (7500,11800,0)
  Subdivisions = 0
  type = Beam
FEATURE [Part::Part2DObjectPython] Line048  # Draft 2D object (typed FeaturePython)
  Area = 0
  ChamferSize = 0
  Closed = false
  End = (7500,23600,0)
  FilletRadius = 0
  Length = 5650
  MakeFace = true
  Points = (2) [(7500,17950,0),(7500,23600,0)]
  Start = (7500,17950,0)
  Subdivisions = 0
  type = Beam
FEATURE [Part::Part2DObjectPython] Line049  # Draft 2D object (typed FeaturePython)
  Area = 0
  ChamferSize = 0
  Closed = false
  End = (18000,0,0)
  FilletRadius = 0
  Length = 5960.91
  MakeFace = true
  Points = (2) [(16100,5650,0),(18000,0,0)]
  Start = (16100,5650,0)
  Subdivisions = 0
  type = Beam
FEATURE [Part::Part2DObjectPython] Line050  # Draft 2D object (typed FeaturePython)
  Area = 0
  ChamferSize = 0
  Closed = false
  End = (16100,11800,0)
  FilletRadius = 0
  Length = 6150
  MakeFace = true
  Points = (2) [(16100,5650,0),(16100,11800,0)]
  Start = (16100,5650,0)
  Subdivisions = 0
  type = Beam
FEATURE [Part::Part2DObjectPython] Line051  # Draft 2D object (typed FeaturePython)
  Area = 0
  ChamferSize = 0
  Closed = false
  End = (16100,17950,0)
  FilletRadius = 0
  Length = 6150
  MakeFace = true
  Points = (2) [(16100,11800,0),(16100,17950,0)]
  Start = (16100,11800,0)
  Subdivisions = 0
  type = Beam
FEATURE [Part::Part2DObjectPython] Line052  # Draft 2D object (typed FeaturePython)
  Area = 0
  ChamferSize = 0
  Closed = false
  End = (16100,23600,0)
  FilletRadius = 0
  Length = 5650
  MakeFace = true
  Points = (2) [(16100,17950,0),(16100,23600,0)]
  Start = (16100,17950,0)
  Subdivisions = 0
  type = Beam
FEATURE [Part::Part2DObjectPython] Line053  # Draft 2D object (typed FeaturePython)
  Area = 0
  ChamferSize = 0
  Closed = false
  End = (11800,5650,0)
  FilletRadius = 0
  Length = 5650
  MakeFace = true
  Points = (2) [(11800,0,0),(11800,5650,0)]
  Start = (11800,0,0)
  Subdivisions = 0
  type = Beam
FEATURE [App::DocumentObjectGroup] Beams
  Group = -> [Line021,Line022,Line023,Line024,Line025,Line026,Line027,Line028,Line029,Line030,Line031,Line032,Line033,Line034,Line035,Line036,Line037,Line038,Line039,Line040,Line041,Line042,Line043,Line044,Line045,Line046,Line047,Line048,Line049,Line050,Line051,Line052,Line053]
FEATURE [App::FeaturePython] Safe  # WARN: FeaturePython — macro-defined, semantics opaque (R4)
  input = <path>
  input_str = <blob: 80278 chars omitted>
  output = <path>
FEATURE [Part::Part2DObjectPython] Wire  # Draft 2D object (typed FeaturePython)
  Area = 0
  ChamferSize = 0
  Closed = false
  End = (23600,0,0)
  FilletRadius = 0
  Length = 23600
  MakeFace = false
  Points = (5) [(0,0,0),(5600,0,0),(11800,0,0),(18000,0,0),(23600,0,0)]
  Start = (0,0,0)
  Subdivisions = 0
FEATURE [Part::FeaturePython] BaseFoundation  # Arch/BIM 77 (typed FeaturePython)
  Base = -> Wire
  HorizontalArea = 0
  IfcData = attributes={"GlobalId": {"name": "GlobalId", "type": "IfcGloballyUniqueId", "is_enum": false, "enum_values": []}, "Description": {"... (+511 chars omitted),+1 more (map truncated)
  IfcType = 77
  MoveBase = false
  MoveWithHost = false
  PerimeterLength = 0
  PredefinedType = 0
  VerticalArea = 0
  align = 0
  design_type = 0
  fc = 25000
  final_wire_first_point = (0,0,0)
  final_wire_last_point = (0,0,0)
  height = 600
  ks = 2
  layer = 0
  left_width = 400
  right_width = 400
  width = 800
FEATURE [Part::Part2DObjectPython] Wire001  # Draft 2D object (typed FeaturePython)
  Area = 0
  ChamferSize = 0
  Closed = false
  End = (0,23600,0)
  FilletRadius = 0
  Length = 23600
  MakeFace = false
  Points = (5) [(0,0,0),(0,5650,0),(0,11800,0),(0,17950,0),(0,23600,0)]
  Start = (0,0,0)
  Subdivisions = 0
FEATURE [Part::FeaturePython] BaseFoundation001  # Arch/BIM 77 (typed FeaturePython)
  Base = -> Wire001
  HorizontalArea = 0
  IfcData = attributes={"GlobalId": {"name": "GlobalId", "type": "IfcGloballyUniqueId", "is_enum": false, "enum_values": []}, "Description": {"... (+511 chars omitted),+1 more (map truncated)
  IfcType = 77
  MoveBase = false
  MoveWithHost = false
  PerimeterLength = 0
  PredefinedType = 0
  VerticalArea = 0
  align = 0
  design_type = 0
  fc = 25000
  final_wire_first_point = (0,0,0)
  final_wire_last_point = (0,0,0)
  height = 600
  ks = 2
  layer = 1
  left_width = 400
  right_width = 400
  width = 800
FEATURE [Part::Part2DObjectPython] Wire002  # Draft 2D object (typed FeaturePython)
  Area = 0
  ChamferSize = 0
  Closed = false
  End = (23600,5650,0)
  FilletRadius = 0
  Length = 23600
  MakeFace = false
  Points = (4) [(0,5650,0),(7500,5650,0),(16100,5650,0),(23600,5650,0)]
  Start = (0,5650,0)
  Subdivisions = 0
FEATURE [Part::FeaturePython] BaseFoundation002  # Arch/BIM 77 (typed FeaturePython)
  Base = -> Wire002
  HorizontalArea = 0
  IfcData = attributes={"GlobalId": {"name": "GlobalId", "type": "IfcGloballyUniqueId", "is_enum": false, "enum_values": []}, "Description": {"... (+511 chars omitted),+1 more (map truncated)
  IfcType = 77
  MoveBase = false
  MoveWithHost = false
  PerimeterLength = 0
  PredefinedType = 0
  VerticalArea = 0
  align = 0
  design_type = 0
  fc = 25000
  final_wire_first_point = (0,0,0)
  final_wire_last_point = (0,0,0)
  height = 600
  ks = 2
  layer = 0
  left_width = 400
  right_width = 400
  width = 800
FEATURE [Part::Part2DObjectPython] Wire003  # Draft 2D object (typed FeaturePython)
  Area = 0
  ChamferSize = 0
  Closed = false
  End = (23600,11800,0)
  FilletRadius = 0
  Length = 23600
  MakeFace = false
  Points = (4) [(0,11800,0),(7500,11800,0),(16100,11800,0),(23600,11800,0)]
  Start = (0,11800,0)
  Subdivisions = 0
FEATURE [Part::FeaturePython] BaseFoundation003  # Arch/BIM 77 (typed FeaturePython)
  Base = -> Wire003
  HorizontalArea = 0
  IfcData = attributes={"GlobalId": {"name": "GlobalId", "type": "IfcGloballyUniqueId", "is_enum": false, "enum_values": []}, "Description": {"... (+511 chars omitted),+1 more (map truncated)
  IfcType = 77
  MoveBase = false
  MoveWithHost = false
  PerimeterLength = 0
  PredefinedType = 0
  VerticalArea = 0
  align = 0
  design_type = 0
  fc = 25000
  final_wire_first_point = (0,0,0)
  final_wire_last_point = (0,0,0)
  height = 600
  ks = 2
  layer = 0
  left_width = 400
  right_width = 400
  width = 800
FEATURE [Part::Part2DObjectPython] Wire004  # Draft 2D object (typed FeaturePython)
  Area = 0
  ChamferSize = 0
  Closed = false
  End = (23600,17950,0)
  FilletRadius = 0
  Length = 23600
  MakeFace = false
  Points = (4) [(0,17950,0),(7500,17950,0),(16100,17950,0),(23600,17950,0)]
  Start = (0,17950,0)
  Subdivisions = 0
FEATURE [Part::FeaturePython] BaseFoundation004  # Arch/BIM 77 (typed FeaturePython)
  Base = -> Wire004
  HorizontalArea = 0
  IfcData = attributes={"GlobalId": {"name": "GlobalId", "type": "IfcGloballyUniqueId", "is_enum": false, "enum_values": []}, "Description": {"... (+511 chars omitted),+1 more (map truncated)
  IfcType = 77
  MoveBase = false
  MoveWithHost = false
  PerimeterLength = 0
  PredefinedType = 0
  VerticalArea = 0
  align = 0
  design_type = 0
  fc = 25000
  final_wire_first_point = (0,0,0)
  final_wire_last_point = (0,0,0)
  height = 600
  ks = 2
  layer = 0
  left_width = 400
  right_width = 400
  width = 800
FEATURE [Part::Part2DObjectPython] Wire005  # Draft 2D object (typed FeaturePython)
  Area = 0
  ChamferSize = 0
  Closed = false
  End = (23600,23600,0)
  FilletRadius = 0
  Length = 23600
  MakeFace = false
  Points = (4) [(0,23600,0),(7500,23600,0),(16100,23600,0),(23600,23600,0)]
  Start = (0,23600,0)
  Subdivisions = 0
FEATURE [Part::FeaturePython] BaseFoundation005  # Arch/BIM 77 (typed FeaturePython)
  Base = -> Wire005
  HorizontalArea = 0
  IfcData = attributes={"GlobalId": {"name": "GlobalId", "type": "IfcGloballyUniqueId", "is_enum": false, "enum_values": []}, "Description": {"... (+511 chars omitted),+1 more (map truncated)
  IfcType = 77
  MoveBase = false
  MoveWithHost = false
  PerimeterLength = 0
  PredefinedType = 0
  VerticalArea = 0
  align = 0
  design_type = 0
  fc = 25000
  final_wire_first_point = (0,0,0)
  final_wire_last_point = (0,0,0)
  height = 600
  ks = 2
  layer = 0
  left_width = 400
  right_width = 400
  width = 800
FEATURE [Part::Part2DObjectPython] Wire006  # Draft 2D object (typed FeaturePython)
  Area = 0
  ChamferSize = 0
  Closed = false
  End = (7500,23600,0)
  FilletRadius = 0
  Length = 23910.9
  MakeFace = false
  Points = (5) [(5600,0,0),(7500,5650,0),(7500,11800,0),(7500,17950,0),(7500,23600,0)]
  Start = (5600,0,0)
  Subdivisions = 0
FEATURE [Part::FeaturePython] BaseFoundation006  # Arch/BIM 77 (typed FeaturePython)
  Base = -> Wire006
  HorizontalArea = 0
  IfcData = attributes={"GlobalId": {"name": "GlobalId", "type": "IfcGloballyUniqueId", "is_enum": false, "enum_values": []}, "Description": {"... (+511 chars omitted),+1 more (map truncated)
  IfcType = 77
  MoveBase = false
  MoveWithHost = false
  PerimeterLength = 0
  PredefinedType = 0
  VerticalArea = 0
  align = 0
  design_type = 0
  fc = 25000
  final_wire_first_point = (0,0,0)
  final_wire_last_point = (0,0,0)
  height = 600
  ks = 2
  layer = 1
  left_width = 400
  right_width = 400
  width = 800
FEATURE [Part::Part2DObjectPython] Line054  # Draft 2D object (typed FeaturePython)
  Area = 0
  ChamferSize = 0
  Closed = false
  End = (11800,5650,0)
  FilletRadius = 0
  Length = 5650
  MakeFace = false
  Points = (2) [(11800,0,0),(11800,5650,0)]
  Start = (11800,0,0)
  Subdivisions = 0
FEATURE [Part::FeaturePython] BaseFoundation007  # Arch/BIM 77 (typed FeaturePython)
  Base = -> Line054
  HorizontalArea = 0
  IfcData = attributes={"GlobalId": {"name": "GlobalId", "type": "IfcGloballyUniqueId", "is_enum": false, "enum_values": []}, "Description": {"... (+511 chars omitted),+1 more (map truncated)
  IfcType = 77
  MoveBase = false
  MoveWithHost = false
  PerimeterLength = 0
  PredefinedType = 0
  VerticalArea = 0
  align = 0
  design_type = 0
  fc = 25000
  final_wire_first_point = (0,0,0)
  final_wire_last_point = (0,0,0)
  height = 600
  ks = 2
  layer = 1
  left_width = 400
  right_width = 400
  width = 800
FEATURE [Part::Part2DObjectPython] Line055  # Draft 2D object (typed FeaturePython)
  Area = 0
  ChamferSize = 0
  Closed = false
  End = (18000,0,0)
  FilletRadius = 0
  Length = 5960.91
  MakeFace = false
  Points = (2) [(16100,5650,0),(18000,0,0)]
  Start = (16100,5650,0)
  Subdivisions = 0
FEATURE [Part::FeaturePython] BaseFoundation008  # Arch/BIM 77 (typed FeaturePython)
  Base = -> Line055
  HorizontalArea = 0
  IfcData = attributes={"GlobalId": {"name": "GlobalId", "type": "IfcGloballyUniqueId", "is_enum": false, "enum_values": []}, "Description": {"... (+511 chars omitted),+1 more (map truncated)
  IfcType = 77
  MoveBase = false
  MoveWithHost = false
  PerimeterLength = 0
  PredefinedType = 0
  VerticalArea = 0
  align = 0
  design_type = 0
  fc = 25000
  final_wire_first_point = (0,0,0)
  final_wire_last_point = (0,0,0)
  height = 600
  ks = 2
  layer = 1
  left_width = 400
  right_width = 400
  width = 800
FEATURE [Part::Part2DObjectPython] Wire007  # Draft 2D object (typed FeaturePython)
  Area = 0
  ChamferSize = 0
  Closed = false
  End = (16100,23600,0)
  FilletRadius = 0
  Length = 17950
  MakeFace = false
  Points = (4) [(16100,5650,0),(16100,11800,0),(16100,17950,0),(16100,23600,0)]
  Start = (16100,5650,0)
  Subdivisions = 0
FEATURE [Part::FeaturePython] BaseFoundation009  # Arch/BIM 77 (typed FeaturePython)
  Base = -> Wire007
  HorizontalArea = 0
  IfcData = attributes={"GlobalId": {"name": "GlobalId", "type": "IfcGloballyUniqueId", "is_enum": false, "enum_values": []}, "Description": {"... (+511 chars omitted),+1 more (map truncated)
  IfcType = 77
  MoveBase = false
  MoveWithHost = false
  PerimeterLength = 0
  PredefinedType = 0
  VerticalArea = 0
  align = 0
  design_type = 0
  fc = 25000
  final_wire_first_point = (0,0,0)
  final_wire_last_point = (0,0,0)
  height = 600
  ks = 2
  layer = 1
  left_width = 400
  right_width = 400
  width = 800
FEATURE [Part::Part2DObjectPython] Wire008  # Draft 2D object (typed FeaturePython)
  Area = 0
  ChamferSize = 0
  Closed = false
  End = (23600,23600,0)
  FilletRadius = 0
  Length = 23600
  MakeFace = false
  Points = (5) [(23600,0,0),(23600,5650,0),(23600,11800,0),(23600,17950,0),(23600,23600,0)]
  Start = (23600,0,0)
  Subdivisions = 0
FEATURE [Part::FeaturePython] BaseFoundation010  # Arch/BIM 77 (typed FeaturePython)
  Base = -> Wire008
  HorizontalArea = 0
  IfcData = attributes={"GlobalId": {"name": "GlobalId", "type": "IfcGloballyUniqueId", "is_enum": false, "enum_values": []}, "Description": {"... (+511 chars omitted),+1 more (map truncated)
  IfcType = 77
  MoveBase = false
  MoveWithHost = false
  PerimeterLength = 0
  PredefinedType = 0
  VerticalArea = 0
  align = 0
  design_type = 0
  fc = 25000
  final_wire_first_point = (0,0,0)
  final_wire_last_point = (0,0,0)
  height = 600
  ks = 2
  layer = 1
  left_width = 400
  right_width = 400
  width = 800
FEATURE [Part::FeaturePython] Foundation  # Arch/BIM 77 (typed FeaturePython)
  HorizontalArea = 0
  IfcType = 77
  MoveBase = false
  MoveWithHost = false
  PerimeterLength = 0
  VerticalArea = 0
  base_foundations = -> [BaseFoundation,BaseFoundation001,BaseFoundation002,BaseFoundation003,BaseFoundation004,BaseFoundation005,BaseFoundation006,BaseFoundation007,BaseFoundation008,BaseFoundation009,BaseFoundation010]
  continuous_layer = 0
  cover = 75
  d = 525
  fc = 25000
  foundation_type = 0
  height = 600
  height_punch = 600
  ks = 2
  level = 0
  redraw = false
  split = true
  volume = 100.707
FEATURE [Part::Part2DObjectPython] Line056  # Draft 2D object (typed FeaturePython)
  Area = 0
  ChamferSize = 0
  Closed = false
  End = (24000,0,0)
  FilletRadius = 0
  Length = 24400
  MakeFace = false
  Points = (2) [(-400,0,0),(24000,0,0)]
  Start = (-400,0,0)
  Subdivisions = 0
FEATURE [Part::FeaturePython] Strip  label="CSA1"  # Arch/BIM 0 (typed FeaturePython)
  Base = -> Line056
  HorizontalArea = 0
  IfcData = attributes={"GlobalId": {"name": "GlobalId", "type": "IfcGloballyUniqueId", "is_enum": false, "enum_values": []}, "Description": {"... (+538 chars omitted),+1 more (map truncated)
  IfcType = 0
  MoveBase = false
  MoveWithHost = false
  PerimeterLength = 0
  PredefinedType = 0
  VerticalArea = 0
  align = 0
  design_type = 0
  layer = 0
  left_width = 400
  right_width = 400
  width = 800
FEATURE [Part::Part2DObjectPython] Line057  # Draft 2D object (typed FeaturePython)
  Area = 0
  ChamferSize = 0
  Closed = false
  End = (0,24000,0)
  FilletRadius = 0
  Length = 24400
  MakeFace = false
  Points = (2) [(0,-400,0),(0,24000,0)]
  Start = (0,-400,0)
  Subdivisions = 0
FEATURE [Part::FeaturePython] Strip001  label="CSB1"  # Arch/BIM 0 (typed FeaturePython)
  Base = -> Line057
  HorizontalArea = 0
  IfcData = attributes={"GlobalId": {"name": "GlobalId", "type": "IfcGloballyUniqueId", "is_enum": false, "enum_values": []}, "Description": {"... (+538 chars omitted),+1 more (map truncated)
  IfcType = 0
  MoveBase = false
  MoveWithHost = false
  PerimeterLength = 0
  PredefinedType = 0
  VerticalArea = 0
  align = 0
  design_type = 0
  layer = 1
  left_width = 400
  right_width = 400
  width = 800
FEATURE [Part::Part2DObjectPython] Line058  # Draft 2D object (typed FeaturePython)
  Area = 0
  ChamferSize = 0
  Closed = false
  End = (24000,5650,0)
  FilletRadius = 0
  Length = 24400
  MakeFace = false
  Points = (2) [(-400,5650,0),(24000,5650,0)]
  Start = (-400,5650,0)
  Subdivisions = 0
FEATURE [Part::FeaturePython] Strip002  label="CSA2"  # Arch/BIM 0 (typed FeaturePython)
  Base = -> Line058
  HorizontalArea = 0
  IfcData = attributes={"GlobalId": {"name": "GlobalId", "type": "IfcGloballyUniqueId", "is_enum": false, "enum_values": []}, "Description": {"... (+538 chars omitted),+1 more (map truncated)
  IfcType = 0
  MoveBase = false
  MoveWithHost = false
  PerimeterLength = 0
  PredefinedType = 0
  VerticalArea = 0
  align = 0
  design_type = 0
  layer = 0
  left_width = 400
  right_width = 400
  width = 800
FEATURE [Part::Part2DObjectPython] Line059  # Draft 2D object (typed FeaturePython)
  Area = 0
  ChamferSize = 0
  Closed = false
  End = (24000,11800,0)
  FilletRadius = 0
  Length = 24400
  MakeFace = false
  Points = (2) [(-400,11800,0),(24000,11800,0)]
  Start = (-400,11800,0)
  Subdivisions = 0
FEATURE [Part::FeaturePython] Strip003  label="CSA3"  # Arch/BIM 0 (typed FeaturePython)
  Base = -> Line059
  HorizontalArea = 0
  IfcData = attributes={"GlobalId": {"name": "GlobalId", "type": "IfcGloballyUniqueId", "is_enum": false, "enum_values": []}, "Description": {"... (+538 chars omitted),+1 more (map truncated)
  IfcType = 0
  MoveBase = false
  MoveWithHost = false
  PerimeterLength = 0
  PredefinedType = 0
  VerticalArea = 0
  align = 0
  design_type = 0
  layer = 0
  left_width = 400
  right_width = 400
  width = 800
FEATURE [Part::Part2DObjectPython] Line060  # Draft 2D object (typed FeaturePython)
  Area = 0
  ChamferSize = 0
  Closed = false
  End = (24000,17950,0)
  FilletRadius = 0
  Length = 24400
  MakeFace = false
  Points = (2) [(-400,17950,0),(24000,17950,0)]
  Start = (-400,17950,0)
  Subdivisions = 0
FEATURE [Part::FeaturePython] Strip004  label="CSA4"  # Arch/BIM 0 (typed FeaturePython)
  Base = -> Line060
  HorizontalArea = 0
  IfcData = attributes={"GlobalId": {"name": "GlobalId", "type": "IfcGloballyUniqueId", "is_enum": false, "enum_values": []}, "Description": {"... (+538 chars omitted),+1 more (map truncated)
  IfcType = 0
  MoveBase = false
  MoveWithHost = false
  PerimeterLength = 0
  PredefinedType = 0
  VerticalArea = 0
  align = 0
  design_type = 0
  layer = 0
  left_width = 400
  right_width = 400
  width = 800
FEATURE [Part::Part2DObjectPython] Line061  # Draft 2D object (typed FeaturePython)
  Area = 0
  ChamferSize = 0
  Closed = false
  End = (24000,23600,0)
  FilletRadius = 0
  Length = 24400
  MakeFace = false
  Points = (2) [(-400,23600,0),(24000,23600,0)]
  Start = (-400,23600,0)
  Subdivisions = 0
FEATURE [Part::FeaturePython] Strip005  label="CSA5"  # Arch/BIM 0 (typed FeaturePython)
  Base = -> Line061
  HorizontalArea = 0
  IfcData = attributes={"GlobalId": {"name": "GlobalId", "type": "IfcGloballyUniqueId", "is_enum": false, "enum_values": []}, "Description": {"... (+538 chars omitted),+1 more (map truncated)
  IfcType = 0
  MoveBase = false
  MoveWithHost = false
  PerimeterLength = 0
  PredefinedType = 0
  VerticalArea = 0
  align = 0
  design_type = 0
  layer = 0
  left_width = 400
  right_width = 400
  width = 800
FEATURE [App::DocumentObjectGroup] A_strips
  Group = -> [Strip,Strip002,Strip003,Strip004,Strip005]
FEATURE [Part::Part2DObjectPython] Wire009  # Draft 2D object (typed FeaturePython)
  Area = 0
  ChamferSize = 0
  Closed = false
  End = (7500,24000,0)
  FilletRadius = 0
  Length = 24732.9
  MakeFace = false
  Points = (3) [(5465.49,-400,0),(7500,5650,0),(7500,24000,0)]
  Start = (5465.49,-400,0)
  Subdivisions = 0
FEATURE [Part::FeaturePython] Strip006  label="CSB2"  # Arch/BIM 0 (typed FeaturePython)
  Base = -> Wire009
  HorizontalArea = 0
  IfcData = attributes={"GlobalId": {"name": "GlobalId", "type": "IfcGloballyUniqueId", "is_enum": false, "enum_values": []}, "Description": {"... (+538 chars omitted),+1 more (map truncated)
  IfcType = 0
  MoveBase = false
  MoveWithHost = false
  PerimeterLength = 0
  PredefinedType = 0
  VerticalArea = 0
  align = 0
  design_type = 0
  layer = 1
  left_width = 400
  right_width = 400
  width = 800
FEATURE [Part::Part2DObjectPython] Line062  # Draft 2D object (typed FeaturePython)
  Area = 0
  ChamferSize = 0
  Closed = false
  End = (11800,6050,0)
  FilletRadius = 0
  Length = 6450
  MakeFace = false
  Points = (2) [(11800,-400,0),(11800,6050,0)]
  Start = (11800,-400,0)
  Subdivisions = 0
FEATURE [Part::FeaturePython] Strip007  label="CSB3"  # Arch/BIM 0 (typed FeaturePython)
  Base = -> Line062
  HorizontalArea = 0
  IfcData = attributes={"GlobalId": {"name": "GlobalId", "type": "IfcGloballyUniqueId", "is_enum": false, "enum_values": []}, "Description": {"... (+538 chars omitted),+1 more (map truncated)
  IfcType = 0
  MoveBase = false
  MoveWithHost = false
  PerimeterLength = 0
  PredefinedType = 0
  VerticalArea = 0
  align = 0
  design_type = 0
  layer = 1
  left_width = 400
  right_width = 400
  width = 800
FEATURE [Part::Part2DObjectPython] Line063  # Draft 2D object (typed FeaturePython)
  Area = 0
  ChamferSize = 0
  Closed = false
  End = (18134.5,-400,0)
  FilletRadius = 0
  Length = 6804.94
  MakeFace = false
  Points = (2) [(15965.5,6050,0),(18134.5,-400,0)]
  Start = (15965.5,6050,0)
  Subdivisions = 0
FEATURE [Part::FeaturePython] Strip008  label="CSB4"  # Arch/BIM 0 (typed FeaturePython)
  Base = -> Line063
  HorizontalArea = 0
  IfcData = attributes={"GlobalId": {"name": "GlobalId", "type": "IfcGloballyUniqueId", "is_enum": false, "enum_values": []}, "Description": {"... (+538 chars omitted),+1 more (map truncated)
  IfcType = 0
  MoveBase = false
  MoveWithHost = false
  PerimeterLength = 0
  PredefinedType = 0
  VerticalArea = 0
  align = 0
  design_type = 0
  layer = 1
  left_width = 400
  right_width = 400
  width = 800
FEATURE [Part::Part2DObjectPython] Line064  # Draft 2D object (typed FeaturePython)
  Area = 0
  ChamferSize = 0
  Closed = false
  End = (16100,24000,0)
  FilletRadius = 0
  Length = 18750
  MakeFace = false
  Points = (2) [(16100,5250,0),(16100,24000,0)]
  Start = (16100,5250,0)
  Subdivisions = 0
FEATURE [Part::FeaturePython] Strip009  label="CSB5"  # Arch/BIM 0 (typed FeaturePython)
  Base = -> Line064
  HorizontalArea = 0
  IfcData = attributes={"GlobalId": {"name": "GlobalId", "type": "IfcGloballyUniqueId", "is_enum": false, "enum_values": []}, "Description": {"... (+538 chars omitted),+1 more (map truncated)
  IfcType = 0
  MoveBase = false
  MoveWithHost = false
  PerimeterLength = 0
  PredefinedType = 0
  VerticalArea = 0
  align = 0
  design_type = 0
  layer = 1
  left_width = 400
  right_width = 400
  width = 800
FEATURE [Part::Part2DObjectPython] Line065  # Draft 2D object (typed FeaturePython)
  Area = 0
  ChamferSize = 0
  Closed = false
  End = (23600,24000,0)
  FilletRadius = 0
  Length = 24400
  MakeFace = false
  Points = (2) [(23600,-400,0),(23600,24000,0)]
  Start = (23600,-400,0)
  Subdivisions = 0
FEATURE [Part::FeaturePython] Strip010  label="CSB6"  # Arch/BIM 0 (typed FeaturePython)
  Base = -> Line065
  HorizontalArea = 0
  IfcData = attributes={"GlobalId": {"name": "GlobalId", "type": "IfcGloballyUniqueId", "is_enum": false, "enum_values": []}, "Description": {"... (+538 chars omitted),+1 more (map truncated)
  IfcType = 0
  MoveBase = false
  MoveWithHost = false
  PerimeterLength = 0
  PredefinedType = 0
  VerticalArea = 0
  align = 0
  design_type = 0
  layer = 1
  left_width = 400
  right_width = 400
  width = 800
FEATURE [App::DocumentObjectGroup] B_strips
  Group = -> [Strip001,Strip006,Strip007,Strip008,Strip009,Strip010]
FEATURE [App::FeaturePython] Text  # WARN: FeaturePython — macro-defined, semantics opaque (R4)
  Placement = pos=(-400,23568.8,3900) rot=(0,0,1;0rad)
  Text = Corner 4 | 0.26
FEATURE [Part::FeaturePython] Punch  # WARN: FeaturePython — macro-defined, semantics opaque (R4)
  Area = 840000
  Av = 400
  Fys = 340000
  I22 = 76967187500
  I23 = 0
  I33 = 76967187500
  Location = 3
  Ratio = 0.26
  Use_Reinforcement = false
  Vc = 1050000000
  Vs = 0
  Vu = 277200000
  alpha_s = 20
  angle = 0
  b0 = 1600
  bx = 400
  by = 400
  center_of_column = (1.42e-14,23600,0)
  center_of_load = (1.42e-14,23600,0)
  center_of_punch = (231.25,23368.8,-262.5)
  column = -> Structure
  combos_ratio = COMB1=0.15,COMB10=0.20,COMB11=0.15,COMB12=0.23,COMB13=0.20,COMB14=0.19,COMB15=0.14,COMB16=0.26,COMB17=0.23,COMB18=0.22,COMB19=0.17,COMB2=0.13,+25 more (map truncated)
  d = 525
  fc = 25000
  foundation = -> Foundation
  gamma_vx = 0.4
  gamma_vy = 0.4
  id = C21_Roof
  one_way_shear_capacity = 525000000
  s = 0
  text = -> Text
  user_location = false
  vc = 1250
  x = 0
FEATURE [App::FeaturePython] Text001  # WARN: FeaturePython — macro-defined, semantics opaque (R4)
  Placement = pos=(7500,24000,3900) rot=(0,0,1;0rad)
  Text = Edge 3 | 0.54
FEATURE [Part::FeaturePython] Punch001  # WARN: FeaturePython — macro-defined, semantics opaque (R4)
  Area = 1260000
  Av = 400
  Fys = 340000
  I22 = 137637500000
  I23 = 7.35437e+10
  I33 = 252678125000
  Location = 6
  Ratio = 0.54
  Use_Reinforcement = false
  Vc = 1575000000
  Vs = 0
  Vu = 844200000
  alpha_s = 30
  angle = 0
  b0 = 2400
  bx = 500
  by = 500
  center_of_column = (7500,23600,0)
  center_of_load = (7500,23600,0)
  center_of_punch = (7500,23429.2,-262.5)
  column = -> Structure001
  combos_ratio = COMB1=0.34,COMB10=0.43,COMB11=0.52,COMB12=0.43,COMB13=0.53,COMB14=0.30,COMB15=0.33,COMB16=0.41,COMB17=0.51,COMB18=0.30,COMB19=0.34,COMB2=0.31,+25 more (map truncated)
  d = 525
  fc = 25000
  foundation = -> Foundation
  gamma_vx = 0.4
  gamma_vy = 0.4
  id = C22_Roof
  one_way_shear_capacity = 787500000
  s = 0
  text = -> Text001
  user_location = false
  vc = 1250
  x = 0
FEATURE [App::FeaturePython] Text002  # WARN: FeaturePython — macro-defined, semantics opaque (R4)
  Placement = pos=(16100,24000,3900) rot=(0,0,1;0rad)
  Text = Edge 3 | 0.49
FEATURE [Part::FeaturePython] Punch002  # WARN: FeaturePython — macro-defined, semantics opaque (R4)
  Area = 1.26e+06
  Av = 400
  Fys = 340000
  I22 = 1.37637e+11
  I23 = 7.35438e+10
  I33 = 2.52678e+11
  Location = 6
  Ratio = 0.49
  Use_Reinforcement = false
  Vc = 1.575e+09
  Vs = 0
  Vu = 7.686e+08
  alpha_s = 30
  angle = 0
  b0 = 2400
  bx = 500
  by = 500
  center_of_column = (16100,23600,0)
  center_of_load = (16100,23600,0)
  center_of_punch = (16100,23429.2,-262.5)
  column = -> Structure002
  combos_ratio = COMB1=0.28,COMB10=0.36,COMB11=0.44,COMB12=0.37,COMB13=0.47,COMB14=0.33,COMB15=0.35,COMB16=0.34,COMB17=0.42,COMB18=0.30,COMB19=0.34,COMB2=0.26,+25 more (map truncated)
  d = 525
  fc = 25000
  foundation = -> Foundation
  gamma_vx = 0.4
  gamma_vy = 0.4
  id = C23_Roof
  one_way_shear_capacity = 7.875e+08
  s = 0
  text = -> Text002
  user_location = false
  vc = 1250
  x = 0
FEATURE [App::FeaturePython] Text003  # WARN: FeaturePython — macro-defined, semantics opaque (R4)
  Placement = pos=(24000,23568.8,3900) rot=(0,0,1;0rad)
  Text = Corner 3 | 0.28
FEATURE [Part::FeaturePython] Punch003  # WARN: FeaturePython — macro-defined, semantics opaque (R4)
  Area = 840000
  Av = 400
  Fys = 340000
  I22 = 76967187500
  I23 = 0
  I33 = 76967187500
  Location = 2
  Ratio = 0.28
  Use_Reinforcement = false
  Vc = 1050000000
  Vs = 0
  Vu = 294000000
  alpha_s = 20
  angle = 0
  b0 = 1600
  bx = 400
  by = 400
  center_of_column = (23600,23600,0)
  center_of_load = (23600,23600,0)
  center_of_punch = (23368.8,23368.8,-262.5)
  column = -> Structure003
  combos_ratio = COMB1=0.18,COMB10=0.17,COMB11=0.22,COMB12=0.24,COMB13=0.28,COMB14=0.14,COMB15=0.19,COMB16=0.22,COMB17=0.25,COMB18=0.11,COMB19=0.16,COMB2=0.16,+25 more (map truncated)
  d = 525
  fc = 25000
  foundation = -> Foundation
  gamma_vx = 0.4
  gamma_vy = 0.4
  id = C24_Roof
  one_way_shear_capacity = 525000000
  s = 0
  text = -> Text003
  user_location = false
  vc = 1250
  x = 0
FEATURE [App::FeaturePython] Text004  # WARN: FeaturePython — macro-defined, semantics opaque (R4)
  Placement = pos=(-400,17950,3900) rot=(0,0,1;0rad)
  Text = Edge 4 | 0.42
FEATURE [Part::FeaturePython] Punch004  # WARN: FeaturePython — macro-defined, semantics opaque (R4)
  Area = 1260000
  Av = 400
  Fys = 340000
  I22 = 211728125000
  I23 = 5.98938e+10
  I33 = 123987500000
  Location = 7
  Ratio = 0.42
  Use_Reinforcement = false
  Vc = 1575000000
  Vs = 0
  Vu = 655200000
  alpha_s = 30
  angle = 0
  b0 = 2400
  bx = 400
  by = 400
  center_of_column = (1.42e-14,17950,0)
  center_of_load = (1.42e-14,17950,0)
  center_of_punch = (154.167,17950,-262.5)
  column = -> Structure004
  combos_ratio = COMB1=0.30,COMB10=0.33,COMB11=0.39,COMB12=0.36,COMB13=0.41,COMB14=0.24,COMB15=0.23,COMB16=0.38,COMB17=0.42,COMB18=0.26,COMB19=0.24,COMB2=0.28,+25 more (map truncated)
  d = 525
  fc = 25000
  foundation = -> Foundation
  gamma_vx = 0.4
  gamma_vy = 0.4
  id = C17_Roof
  one_way_shear_capacity = 787500000
  s = 0
  text = -> Text004
  user_location = false
  vc = 1250
  x = 0
FEATURE [App::FeaturePython] Text005  # WARN: FeaturePython — macro-defined, semantics opaque (R4)
  Placement = pos=(7500,18437.5,3900) rot=(0,0,1;0rad)
  Text = Interior | 0.33
FEATURE [Part::FeaturePython] Punch005  # WARN: FeaturePython — macro-defined, semantics opaque (R4)
  Area = 1680000
  Av = 400
  Fys = 340000
  I22 = 263725000000
  I23 = 0
  I33 = 263725000000
  Location = 8
  Ratio = 0.33
  Use_Reinforcement = false
  Vc = 2100000000
  Vs = 0
  Vu = 688800000
  alpha_s = 40
  angle = 0
  b0 = 3200
  bx = 450
  by = 450
  center_of_column = (7500,17950,0)
  center_of_load = (7500,17950,0)
  center_of_punch = (7500,17950,-262.5)
  column = -> Structure005
  combos_ratio = COMB1=0.26,COMB10=0.30,COMB11=0.30,COMB12=0.32,COMB13=0.32,COMB14=0.29,COMB15=0.30,COMB16=0.33,COMB17=0.32,COMB18=0.30,COMB19=0.30,COMB2=0.25,+25 more (map truncated)
  d = 525
  fc = 25000
  foundation = -> Foundation
  gamma_vx = 0.4
  gamma_vy = 0.4
  id = C18_Roof
  one_way_shear_capacity = 1050000000
  s = 0
  text = -> Text005
  user_location = false
  vc = 1250
  x = 0
FEATURE [App::FeaturePython] Text006  # WARN: FeaturePython — macro-defined, semantics opaque (R4)
  Placement = pos=(16100,18437.5,3900) rot=(0,0,1;0rad)
  Text = Interior | 0.29
FEATURE [Part::FeaturePython] Punch006  # WARN: FeaturePython — macro-defined, semantics opaque (R4)
  Area = 1.68e+06
  Av = 400
  Fys = 340000
  I22 = 2.63725e+11
  I23 = 0.00148975
  I33 = 2.63725e+11
  Location = 8
  Ratio = 0.29
  Use_Reinforcement = false
  Vc = 2.1e+09
  Vs = 0
  Vu = 6.048e+08
  alpha_s = 40
  angle = 0
  b0 = 3200
  bx = 450
  by = 450
  center_of_column = (16100,17950,0)
  center_of_load = (16100,17950,0)
  center_of_punch = (16100,17950,-262.5)
  column = -> Structure006
  combos_ratio = COMB1=0.24,COMB10=0.27,COMB11=0.27,COMB12=0.29,COMB13=0.29,COMB14=0.28,COMB15=0.28,COMB16=0.28,COMB17=0.28,COMB18=0.28,COMB19=0.27,COMB2=0.22,+25 more (map truncated)
  d = 525
  fc = 25000
  foundation = -> Foundation
  gamma_vx = 0.4
  gamma_vy = 0.4
  id = C19_Roof
  one_way_shear_capacity = 1.05e+09
  s = 0
  text = -> Text006
  user_location = false
  vc = 1250
  x = 0
FEATURE [App::FeaturePython] Text007  # WARN: FeaturePython — macro-defined, semantics opaque (R4)
  Placement = pos=(24000,17950,3900) rot=(0,0,1;0rad)
  Text = Edge 2 | 0.29
FEATURE [Part::FeaturePython] Punch007  # WARN: FeaturePython — macro-defined, semantics opaque (R4)
  Area = 1260000
  Av = 400
  Fys = 340000
  I22 = 211728125000
  I23 = 5.98938e+10
  I33 = 123987500000
  Location = 5
  Ratio = 0.29
  Use_Reinforcement = false
  Vc = 1575000000
  Vs = 0
  Vu = 453600000
  alpha_s = 30
  angle = 0
  b0 = 2400
  bx = 400
  by = 400
  center_of_column = (23600,17950,0)
  center_of_load = (23600,17950,0)
  center_of_punch = (23445.8,17950,-262.5)
  column = -> Structure007
  combos_ratio = COMB1=0.19,COMB10=0.19,COMB11=0.21,COMB12=0.23,COMB13=0.22,COMB14=0.24,COMB15=0.29,COMB16=0.22,COMB17=0.22,COMB18=0.22,COMB19=0.26,COMB2=0.18,+25 more (map truncated)
  d = 525
  fc = 25000
  foundation = -> Foundation
  gamma_vx = 0.4
  gamma_vy = 0.4
  id = C20_Roof
  one_way_shear_capacity = 787500000
  s = 0
  text = -> Text007
  user_location = false
  vc = 1250
  x = 0
FEATURE [App::FeaturePython] Text008  # WARN: FeaturePython — macro-defined, semantics opaque (R4)
  Placement = pos=(-400,11800,3900) rot=(0,0,1;0rad)
  Text = Edge 4 | 0.50
FEATURE [Part::FeaturePython] Punch008  # WARN: FeaturePython — macro-defined, semantics opaque (R4)
  Area = 1260000
  Av = 400
  Fys = 340000
  I22 = 211728125000
  I23 = 5.98937e+10
  I33 = 123987500000
  Location = 7
  Ratio = 0.5
  Use_Reinforcement = false
  Vc = 1575000000
  Vs = 0
  Vu = 781200000
  alpha_s = 30
  angle = 0
  b0 = 2400
  bx = 400
  by = 400
  center_of_column = (1.42e-14,11800,0)
  center_of_load = (1.42e-14,11800,0)
  center_of_punch = (154.167,11800,-262.5)
  column = -> Structure008
  combos_ratio = COMB1=0.42,COMB10=0.45,COMB11=0.42,COMB12=0.40,COMB13=0.39,COMB14=0.48,COMB15=0.46,COMB16=0.39,COMB17=0.41,COMB18=0.50,COMB19=0.48,COMB2=0.40,+25 more (map truncated)
  d = 525
  fc = 25000
  foundation = -> Foundation
  gamma_vx = 0.4
  gamma_vy = 0.4
  id = C10_Roof
  one_way_shear_capacity = 787500000
  s = 0
  text = -> Text008
  user_location = false
  vc = 1250
  x = 0
FEATURE [App::FeaturePython] Text009  # WARN: FeaturePython — macro-defined, semantics opaque (R4)
  Placement = pos=(7500,12284.1,3900) rot=(0,0,1;0rad)
  Text = Interior | 0.40
FEATURE [Part::FeaturePython] Punch009  # WARN: FeaturePython — macro-defined, semantics opaque (R4)
  Area = 1680000
  Av = 400
  Fys = 340000
  I22 = 2.60915e+11
  I23 = 0
  I33 = 2.60915e+11
  Location = 8
  Ratio = 0.4
  Use_Reinforcement = false
  Vc = 2100000000
  Vs = 0
  Vu = 840000000
  alpha_s = 40
  angle = 0
  b0 = 3200
  bx = 443.113
  by = 443.113
  center_of_column = (7500,11800,0)
  center_of_load = (7500,11800,0)
  center_of_punch = (7500,11800,-262.5)
  column = -> Structure009
  combos_ratio = COMB1=0.33,COMB10=0.34,COMB11=0.34,COMB12=0.36,COMB13=0.35,COMB14=0.37,COMB15=0.38,COMB16=0.37,COMB17=0.36,COMB18=0.37,COMB19=0.38,COMB2=0.32,+25 more (map truncated)
  d = 525
  fc = 25000
  foundation = -> Foundation
  gamma_vx = 0.4
  gamma_vy = 0.4
  id = C12_Roof
  one_way_shear_capacity = 1050000000
  s = 0
  text = -> Text009
  user_location = false
  vc = 1250
  x = 0
FEATURE [App::FeaturePython] Text010  # WARN: FeaturePython — macro-defined, semantics opaque (R4)
  Placement = pos=(16100,12284.1,3900) rot=(0,0,1;0rad)
  Text = Interior | 0.30
FEATURE [Part::FeaturePython] Punch010  # WARN: FeaturePython — macro-defined, semantics opaque (R4)
  Area = 1.68e+06
  Av = 400
  Fys = 340000
  I22 = 2.60915e+11
  I23 = 0
  I33 = 2.60915e+11
  Location = 8
  Ratio = 0.3
  Use_Reinforcement = false
  Vc = 2.1e+09
  Vs = 0
  Vu = 6.216e+08
  alpha_s = 40
  angle = 0
  b0 = 3200
  bx = 443.113
  by = 443.113
  center_of_column = (16100,11800,0)
  center_of_load = (16100,11800,0)
  center_of_punch = (16100,11800,-262.5)
  column = -> Structure010
  combos_ratio = COMB1=0.26,COMB10=0.28,COMB11=0.28,COMB12=0.30,COMB13=0.30,COMB14=0.29,COMB15=0.29,COMB16=0.29,COMB17=0.29,COMB18=0.29,COMB19=0.28,COMB2=0.24,+25 more (map truncated)
  d = 525
  fc = 25000
  foundation = -> Foundation
  gamma_vx = 0.4
  gamma_vy = 0.4
  id = C13_Roof
  one_way_shear_capacity = 1.05e+09
  s = 0
  text = -> Text010
  user_location = false
  vc = 1250
  x = 0
FEATURE [App::FeaturePython] Text011  # WARN: FeaturePython — macro-defined, semantics opaque (R4)
  Placement = pos=(24000,11800,3900) rot=(0,0,1;0rad)
  Text = Edge 2 | 0.31
FEATURE [Part::FeaturePython] Punch011  # WARN: FeaturePython — macro-defined, semantics opaque (R4)
  Area = 1260000
  Av = 400
  Fys = 340000
  I22 = 211728125000
  I23 = 5.98938e+10
  I33 = 123987500000
  Location = 5
  Ratio = 0.31
  Use_Reinforcement = false
  Vc = 1575000000
  Vs = 0
  Vu = 491400000
  alpha_s = 30
  angle = 0
  b0 = 2400
  bx = 400
  by = 400
  center_of_column = (23600,11800,0)
  center_of_load = (23600,11800,0)
  center_of_punch = (23445.8,11800,-262.5)
  column = -> Structure011
  combos_ratio = COMB1=0.23,COMB10=0.29,COMB11=0.30,COMB12=0.29,COMB13=0.28,COMB14=0.27,COMB15=0.31,COMB16=0.28,COMB17=0.27,COMB18=0.25,COMB19=0.30,COMB2=0.22,+25 more (map truncated)
  d = 525
  fc = 25000
  foundation = -> Foundation
  gamma_vx = 0.4
  gamma_vy = 0.4
  id = C14_Roof
  one_way_shear_capacity = 787500000
  s = 0
  text = -> Text011
  user_location = false
  vc = 1250
  x = 0
FEATURE [App::FeaturePython] Text012  # WARN: FeaturePython — macro-defined, semantics opaque (R4)
  Placement = pos=(-400,5650,3900) rot=(0,0,1;0rad)
  Text = Edge 4 | 0.31
FEATURE [Part::FeaturePython] Punch012  # WARN: FeaturePython — macro-defined, semantics opaque (R4)
  Area = 1260000
  Av = 400
  Fys = 340000
  I22 = 211728125000
  I23 = 5.98937e+10
  I33 = 123987500000
  Location = 7
  Ratio = 0.31
  Use_Reinforcement = false
  Vc = 1575000000
  Vs = 0
  Vu = 491400000
  alpha_s = 30
  angle = 0
  b0 = 2400
  bx = 400
  by = 400
  center_of_column = (1.42e-14,5650,0)
  center_of_load = (1.42e-14,5650,0)
  center_of_punch = (154.167,5650,-262.5)
  column = -> Structure012
  combos_ratio = COMB1=0.21,COMB10=0.24,COMB11=0.30,COMB12=0.25,COMB13=0.29,COMB14=0.22,COMB15=0.21,COMB16=0.27,COMB17=0.31,COMB18=0.22,COMB19=0.22,COMB2=0.19,+25 more (map truncated)
  d = 525
  fc = 25000
  foundation = -> Foundation
  gamma_vx = 0.4
  gamma_vy = 0.4
  id = C6_Roof
  one_way_shear_capacity = 787500000
  s = 0
  text = -> Text012
  user_location = false
  vc = 1250
  x = 0
FEATURE [App::FeaturePython] Text013  # WARN: FeaturePython — macro-defined, semantics opaque (R4)
  Placement = pos=(7500,6137.5,3900) rot=(0,0,1;0rad)
  Text = Interior | 0.30
FEATURE [Part::FeaturePython] Punch013  # WARN: FeaturePython — macro-defined, semantics opaque (R4)
  Area = 1.69736e+06
  Av = 400
  Fys = 340000
  I22 = 2.6704e+11
  I23 = 3.15713e+10
  I33 = 2.72201e+11
  Location = 8
  Ratio = 0.3
  Use_Reinforcement = false
  Vc = 2.1217e+09
  Vs = 0
  Vu = 6.28025e+08
  alpha_s = 40
  angle = 0
  b0 = 3233.07
  bx = 450
  by = 450
  center_of_column = (7500,5650,0)
  center_of_load = (7500,5650,0)
  center_of_punch = (7460.35,5646.2,-262.5)
  column = -> Structure013
  combos_ratio = COMB1=0.25,COMB10=0.29,COMB11=0.29,COMB12=0.29,COMB13=0.29,COMB14=0.27,COMB15=0.27,COMB16=0.30,COMB17=0.29,COMB18=0.28,COMB19=0.27,COMB2=0.23,+25 more (map truncated)
  d = 525
  fc = 25000
  foundation = -> Foundation
  gamma_vx = 0.4
  gamma_vy = 0.4
  id = C7_Roof
  one_way_shear_capacity = 1.06085e+09
  s = 0
  text = -> Text013
  user_location = false
  vc = 1250
  x = 0
FEATURE [App::FeaturePython] Text014  # WARN: FeaturePython — macro-defined, semantics opaque (R4)
  Placement = pos=(16100,6137.5,3900) rot=(0,0,1;0rad)
  Text = Interior | 0.30
FEATURE [Part::FeaturePython] Punch014  # WARN: FeaturePython — macro-defined, semantics opaque (R4)
  Area = 1.69736e+06
  Av = 400
  Fys = 340000
  I22 = 2.6704e+11
  I23 = 3.15713e+10
  I33 = 2.72201e+11
  Location = 8
  Ratio = 0.3
  Use_Reinforcement = false
  Vc = 2.1217e+09
  Vs = 0
  Vu = 6.28025e+08
  alpha_s = 40
  angle = 0
  b0 = 3233.07
  bx = 450
  by = 450
  center_of_column = (16100,5650,0)
  center_of_load = (16100,5650,0)
  center_of_punch = (16139.6,5646.2,-262.5)
  column = -> Structure014
  combos_ratio = COMB1=0.24,COMB10=0.27,COMB11=0.29,COMB12=0.28,COMB13=0.30,COMB14=0.27,COMB15=0.29,COMB16=0.28,COMB17=0.29,COMB18=0.27,COMB19=0.28,COMB2=0.22,+25 more (map truncated)
  d = 525
  fc = 25000
  foundation = -> Foundation
  gamma_vx = 0.4
  gamma_vy = 0.4
  id = C8_Roof
  one_way_shear_capacity = 1.06085e+09
  s = 0
  text = -> Text014
  user_location = false
  vc = 1250
  x = 0
FEATURE [App::FeaturePython] Text015  # WARN: FeaturePython — macro-defined, semantics opaque (R4)
  Placement = pos=(24000,5650,3900) rot=(0,0,1;0rad)
  Text = Edge 2 | 0.29
FEATURE [Part::FeaturePython] Punch015  # WARN: FeaturePython — macro-defined, semantics opaque (R4)
  Area = 1260000
  Av = 400
  Fys = 340000
  I22 = 211728125000
  I23 = 5.98938e+10
  I33 = 123987500000
  Location = 5
  Ratio = 0.29
  Use_Reinforcement = false
  Vc = 1575000000
  Vs = 0
  Vu = 453600000
  alpha_s = 30
  angle = 0
  b0 = 2400
  bx = 400
  by = 400
  center_of_column = (23600,5650,0)
  center_of_load = (23600,5650,0)
  center_of_punch = (23445.8,5650,-262.5)
  column = -> Structure015
  combos_ratio = COMB1=0.20,COMB10=0.19,COMB11=0.21,COMB12=0.23,COMB13=0.22,COMB14=0.25,COMB15=0.29,COMB16=0.22,COMB17=0.21,COMB18=0.24,COMB19=0.28,COMB2=0.18,+25 more (map truncated)
  d = 525
  fc = 25000
  foundation = -> Foundation
  gamma_vx = 0.4
  gamma_vy = 0.4
  id = C9_Roof
  one_way_shear_capacity = 787500000
  s = 0
  text = -> Text015
  user_location = false
  vc = 1250
  x = 0
FEATURE [App::FeaturePython] Text016  # WARN: FeaturePython — macro-defined, semantics opaque (R4)
  Placement = pos=(-400,31.25,3900) rot=(0,0,1;0rad)
  Text = Corner 1 | 0.27
FEATURE [Part::FeaturePython] Punch016  # WARN: FeaturePython — macro-defined, semantics opaque (R4)
  Area = 840000
  Av = 400
  Fys = 340000
  I22 = 76967187500
  I23 = 0
  I33 = 76967187500
  Location = 0
  Ratio = 0.27
  Use_Reinforcement = false
  Vc = 1050000000
  Vs = 0
  Vu = 285600000
  alpha_s = 20
  angle = 0
  b0 = 1600
  bx = 400
  by = 400
  center_of_column = (0,0,0)
  center_of_load = (0,0,0)
  center_of_punch = (231.25,231.25,-262.5)
  column = -> Structure016
  combos_ratio = COMB1=0.15,COMB10=0.16,COMB11=0.20,COMB12=0.11,COMB13=0.17,COMB14=0.21,COMB15=0.24,COMB16=0.14,COMB17=0.19,COMB18=0.24,COMB19=0.27,COMB2=0.14,+25 more (map truncated)
  d = 525
  fc = 25000
  foundation = -> Foundation
  gamma_vx = 0.4
  gamma_vy = 0.4
  id = C1_Roof
  one_way_shear_capacity = 525000000
  s = 0
  text = -> Text016
  user_location = false
  vc = 1250
  x = 0
FEATURE [App::FeaturePython] Text017  # WARN: FeaturePython — macro-defined, semantics opaque (R4)
  Placement = pos=(5600,-400,3900) rot=(0,0,1;0rad)
  Text = Edge 1 | 0.29
FEATURE [Part::FeaturePython] Punch017  # WARN: FeaturePython — macro-defined, semantics opaque (R4)
  Area = 1.25553e+06
  Av = 400
  Fys = 340000
  I22 = 1.23722e+11
  I23 = 6.19547e+10
  I33 = 2.13904e+11
  Location = 4
  Ratio = 0.29
  Use_Reinforcement = false
  Vc = 1.56941e+09
  Vs = 0
  Vu = 4.5199e+08
  alpha_s = 30
  angle = 0
  b0 = 2391.48
  bx = 400
  by = 400
  center_of_column = (5600,1.42e-14,0)
  center_of_load = (5600,1.42e-14,0)
  center_of_punch = (5641.96,152.252,-262.5)
  column = -> Structure017
  combos_ratio = COMB1=0.19,COMB10=0.23,COMB11=0.22,COMB12=0.17,COMB13=0.18,COMB14=0.21,COMB15=0.26,COMB16=0.18,COMB17=0.18,COMB18=0.23,COMB19=0.28,COMB2=0.18,+25 more (map truncated)
  d = 525
  fc = 25000
  foundation = -> Foundation
  gamma_vx = 0.4
  gamma_vy = 0.4
  id = C2_Roof
  one_way_shear_capacity = 7.84705e+08
  s = 0
  text = -> Text017
  user_location = false
  vc = 1250
  x = 0
FEATURE [App::FeaturePython] Text018  # WARN: FeaturePython — macro-defined, semantics opaque (R4)
  Placement = pos=(11800,-400,3900) rot=(0,0,1;0rad)
  Text = Edge 1 | 0.37
FEATURE [Part::FeaturePython] Punch018  # WARN: FeaturePython — macro-defined, semantics opaque (R4)
  Area = 1260000
  Av = 400
  Fys = 340000
  I22 = 123987500000
  I23 = 59893750000
  I33 = 211728125000
  Location = 4
  Ratio = 0.37
  Use_Reinforcement = false
  Vc = 1575000000
  Vs = 0
  Vu = 579600000
  alpha_s = 30
  angle = 0
  b0 = 2400
  bx = 400
  by = 400
  center_of_column = (11800,-1.42e-14,0)
  center_of_load = (11800,-1.42e-14,0)
  center_of_punch = (11800,154.167,-262.5)
  column = -> Structure018
  combos_ratio = COMB1=0.26,COMB10=0.30,COMB11=0.29,COMB12=0.22,COMB13=0.24,COMB14=0.29,COMB15=0.34,COMB16=0.23,COMB17=0.25,COMB18=0.30,COMB19=0.36,COMB2=0.24,+25 more (map truncated)
  d = 525
  fc = 25000
  foundation = -> Foundation
  gamma_vx = 0.4
  gamma_vy = 0.4
  id = C3_Roof
  one_way_shear_capacity = 787500000
  s = 0
  text = -> Text018
  user_location = false
  vc = 1250
  x = 0
FEATURE [App::FeaturePython] Text019  # WARN: FeaturePython — macro-defined, semantics opaque (R4)
  Placement = pos=(18000,-400,3900) rot=(0,0,1;0rad)
  Text = Edge 1 | 0.30
FEATURE [Part::FeaturePython] Punch019  # WARN: FeaturePython — macro-defined, semantics opaque (R4)
  Area = 1.25553e+06
  Av = 400
  Fys = 340000
  I22 = 1.23722e+11
  I23 = 6.19547e+10
  I33 = 2.13904e+11
  Location = 4
  Ratio = 0.3
  Use_Reinforcement = false
  Vc = 1.56941e+09
  Vs = 0
  Vu = 4.771e+08
  alpha_s = 30
  angle = 0
  b0 = 2391.48
  bx = 400
  by = 400
  center_of_column = (18000,1.42e-14,0)
  center_of_load = (18000,1.42e-14,0)
  center_of_punch = (17958,152.252,-262.5)
  column = -> Structure019
  combos_ratio = COMB1=0.19,COMB10=0.22,COMB11=0.22,COMB12=0.17,COMB13=0.19,COMB14=0.22,COMB15=0.29,COMB16=0.17,COMB17=0.19,COMB18=0.24,COMB19=0.30,COMB2=0.18,+25 more (map truncated)
  d = 525
  fc = 25000
  foundation = -> Foundation
  gamma_vx = 0.4
  gamma_vy = 0.4
  id = C4_Roof
  one_way_shear_capacity = 7.84705e+08
  s = 0
  text = -> Text019
  user_location = false
  vc = 1250
  x = 0
FEATURE [App::FeaturePython] Text020  # WARN: FeaturePython — macro-defined, semantics opaque (R4)
  Placement = pos=(24000,31.25,3900) rot=(0,0,1;0rad)
  Text = Corner 2 | 0.26
FEATURE [Part::FeaturePython] Punch020  # WARN: FeaturePython — macro-defined, semantics opaque (R4)
  Area = 840000
  Av = 400
  Fys = 340000
  I22 = 76967187500
  I23 = 0
  I33 = 76967187500
  Location = 1
  Ratio = 0.26
  Use_Reinforcement = false
  Vc = 1050000000
  Vs = 0
  Vu = 268800000
  alpha_s = 20
  angle = 0
  b0 = 1600
  bx = 400
  by = 400
  center_of_column = (23600,-1.42e-14,0)
  center_of_load = (23600,-1.42e-14,0)
  center_of_punch = (23368.8,231.25,-262.5)
  column = -> Structure020
  combos_ratio = COMB1=0.15,COMB10=0.22,COMB11=0.18,COMB12=0.17,COMB13=0.11,COMB14=0.26,COMB15=0.22,COMB16=0.14,COMB17=0.08,COMB18=0.22,COMB19=0.19,COMB2=0.14,+25 more (map truncated)
  d = 525
  fc = 25000
  foundation = -> Foundation
  gamma_vx = 0.4
  gamma_vy = 0.4
  id = C5_Roof
  one_way_shear_capacity = 525000000
  s = 0
  text = -> Text020
  user_location = false
  vc = 1250
  x = 0
FEATURE [App::DocumentObjectGroup] Punches
  Group = -> [Punch,Punch001,Punch002,Punch003,Punch004,Punch005,Punch006,Punch007,Punch008,Punch009,Punch010,Punch011,Punch012,Punch013,Punch014,Punch015,Punch016,Punch017,Punch018,Punch019,Punch020]
note: 2 file-system paths scrubbed to <path> (originals preserved in the JSON sidecar)
